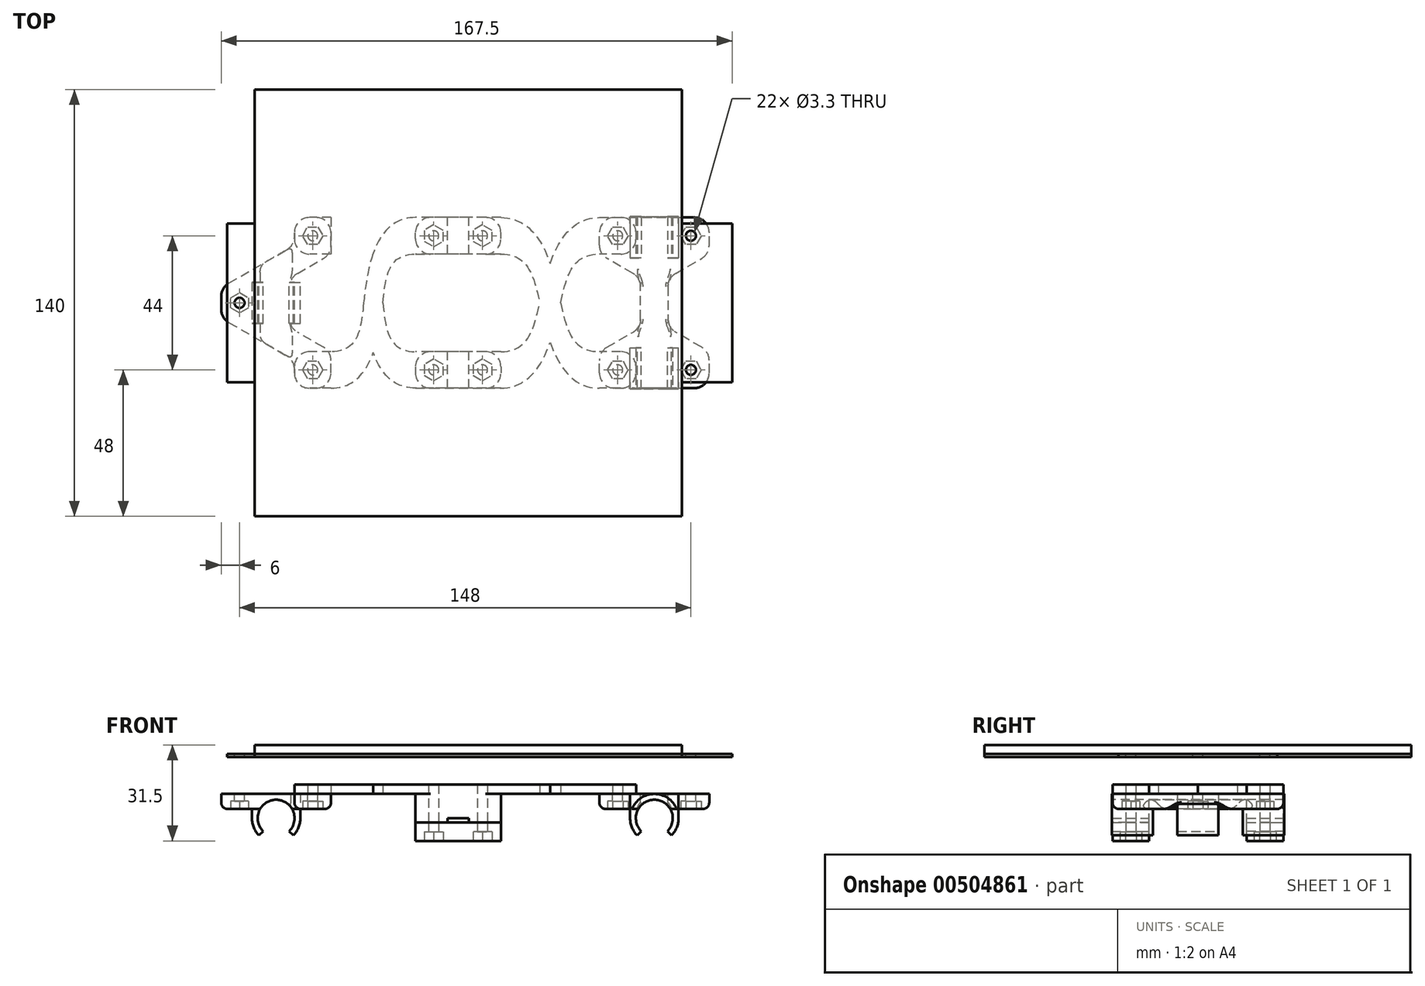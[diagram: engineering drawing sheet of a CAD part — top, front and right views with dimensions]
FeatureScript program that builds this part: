
annotation { "Feature Type Name" : "Feature", "Feature Type Description" : "" }
export const myFeature = defineFeature(function(context is Context, id is Id, definition is map)
    precondition{}
    {
        {
            var Q0;
            Q0=qCreatedBy(makeId("Top.planeOp"),FACE);
            var sketch = newSketch(context, id + "F0", { "sketchPlane" : qUnion([Q0])});
            skLineSegment(sketch, "E0", {"start": v(0, 0) * mm, "end": v(0, -44) * mm});
            skLineSegment(sketch, "E1", {"start": v(0, -44) * mm, "end": v(-9, -44) * mm});
            skLineSegment(sketch, "E2", {"start": v(-9, -44) * mm, "end": v(-9, -96) * mm});
            skLineSegment(sketch, "E3", {"start": v(-9, -96) * mm, "end": v(0, -96) * mm});
            skLineSegment(sketch, "E4", {"start": v(0, -96) * mm, "end": v(0, -140) * mm});
            skLineSegment(sketch, "E5", {"start": v(0, -140) * mm, "end": v(140, -140) * mm});
            skLineSegment(sketch, "E6", {"start": v(140, -140) * mm, "end": v(140, -96) * mm});
            skLineSegment(sketch, "E7", {"start": v(140, -96) * mm, "end": v(156.5, -96) * mm});
            skLineSegment(sketch, "E8", {"start": v(156.5, -96) * mm, "end": v(156.5, -44) * mm});
            skLineSegment(sketch, "E9", {"start": v(156.5, -44) * mm, "end": v(140, -44) * mm});
            skLineSegment(sketch, "E10", {"start": v(140, -44) * mm, "end": v(140, 0) * mm});
            skLineSegment(sketch, "E11", {"start": v(140, 0) * mm, "end": v(0, 0) * mm});
            skLineSegment(sketch, "E12", {"start": v(0, -96) * mm, "end": v(0, -44) * mm});
            skLineSegment(sketch, "E13", {"start": v(140, -96) * mm, "end": v(140, -44) * mm});
            skCircle(sketch, "E14", {"center": v(-5, -70) * mm, "radius": 1.65 * mm});
            skCircle(sketch, "E15", {"center": v(143, -48) * mm, "radius": 1.65 * mm});
            skCircle(sketch, "E16", {"center": v(143, -92) * mm, "radius": 1.65 * mm});
            skSolve(sketch);
        }
        {
            var Q0;
            Q0=makeQuery(id+"F0.imprint","IMPRINT",FACE,{"disambiguationData":[TD([[makeQuery(id+"F0.imprint","IMPRINT",EDGE,{"derivedFrom":sQuery(id+"F0.wireOp",EDGE,"E1")}),1.0]])]});
            var Q1;
            Q1=makeQuery(id+"F0.imprint","IMPRINT",FACE,{"disambiguationData":[TD([[makeQuery(id+"F0.imprint","IMPRINT",EDGE,{"derivedFrom":sQuery(id+"F0.wireOp",EDGE,"E0")}),1.0]])]});
            var Q2;
            Q2=makeQuery(id+"F0.imprint","IMPRINT",FACE,{"disambiguationData":[TD([[makeQuery(id+"F0.imprint","IMPRINT",EDGE,{"derivedFrom":sQuery(id+"F0.wireOp",EDGE,"E7")}),1.0]])]});
            extrude(context, id + "F1", {"entities" : qUnion([Q0, Q1, Q2]), "oppositeDirection" : true, "depth" : 1 * mm});
        }
        {
            var Q0;
            Q0=makeQuery(id+"F0.imprint","IMPRINT",FACE,{"disambiguationData":[TD([[makeQuery(id+"F0.imprint","IMPRINT",EDGE,{"derivedFrom":sQuery(id+"F0.wireOp",EDGE,"E0")}),1.0]])]});
            extrude(context, id + "F2", {"entities" : qUnion([Q0]), "depth" : 3 * mm});
        }
        {
            var Q0;
            Q0=makeQuery(id+"F1.opExtrude","CAP_FACE",FACE,{"disambiguationData":[OSD([sQuery(id+"F0.wireOp",EDGE,"E0"),sQuery(id+"F0.wireOp",EDGE,"E1"),sQuery(id+"F0.wireOp",EDGE,"E2"),sQuery(id+"F0.wireOp",EDGE,"E3"),sQuery(id+"F0.wireOp",EDGE,"E4"),sQuery(id+"F0.wireOp",EDGE,"E5"),sQuery(id+"F0.wireOp",EDGE,"E6"),sQuery(id+"F0.wireOp",EDGE,"E7"),sQuery(id+"F0.wireOp",EDGE,"E8"),sQuery(id+"F0.wireOp",EDGE,"E9"),sQuery(id+"F0.wireOp",EDGE,"E10"),sQuery(id+"F0.wireOp",EDGE,"E11"),sQuery(id+"F0.wireOp",EDGE,"E14"),sQuery(id+"F0.wireOp",EDGE,"E15"),sQuery(id+"F0.wireOp",EDGE,"E16")])],"isStart":false});
            cPlane(context, id + "F3", {"entities" : qUnion([Q0]), "cplaneType" : CPlaneType.OFFSET, "offset" : 12 * mm, "width" : 150 * mm, "height" : 150 * mm});
        }
        {
            var Q0;
            Q0=qCreatedBy(id+"F3.planeOp",FACE);
            var sketch = newSketch(context, id + "F4", { "sketchPlane" : qUnion([Q0])});
            skCircle(sketch, "E17.0", {"center": v(-5, 70) * mm, "radius": 1.65 * mm});
            skCircle(sketch, "E17.1", {"center": v(143, 92) * mm, "radius": 1.65 * mm});
            skCircle(sketch, "E17.2", {"center": v(143, 48) * mm, "radius": 1.65 * mm});
            skCircle(sketch, "E18.cCircle", {"center": v(-5, 70) * mm, "radius": 2.9 * mm, "construction": true});
            skLineSegment(sketch, "E18.0", {"start": v(-2.1, 71.67) * mm, "end": v(-2.1, 68.33) * mm});
            skLineSegment(sketch, "E18.1", {"start": v(-2.1, 68.33) * mm, "end": v(-5, 66.65) * mm});
            skLineSegment(sketch, "E18.2", {"start": v(-5, 66.65) * mm, "end": v(-7.9, 68.33) * mm});
            skLineSegment(sketch, "E18.3", {"start": v(-7.9, 68.33) * mm, "end": v(-7.9, 71.67) * mm});
            skLineSegment(sketch, "E18.4", {"start": v(-7.9, 71.67) * mm, "end": v(-5, 73.35) * mm});
            skLineSegment(sketch, "E18.5", {"start": v(-5, 73.35) * mm, "end": v(-2.1, 71.67) * mm});
            skPoint(sketch, "E18.0.midPoint", {"position": v(-2.1, 70) * mm});
            skCircle(sketch, "E19.cCircle", {"center": v(143, 48) * mm, "radius": 2.9 * mm, "construction": true});
            skLineSegment(sketch, "E19.0", {"start": v(141.33, 50.9) * mm, "end": v(144.67, 50.9) * mm});
            skLineSegment(sketch, "E19.1", {"start": v(144.67, 50.9) * mm, "end": v(146.35, 48) * mm});
            skLineSegment(sketch, "E19.2", {"start": v(146.35, 48) * mm, "end": v(144.67, 45.1) * mm});
            skLineSegment(sketch, "E19.3", {"start": v(144.67, 45.1) * mm, "end": v(141.33, 45.1) * mm});
            skLineSegment(sketch, "E19.4", {"start": v(141.33, 45.1) * mm, "end": v(139.65, 48) * mm});
            skLineSegment(sketch, "E19.5", {"start": v(139.65, 48) * mm, "end": v(141.33, 50.9) * mm});
            skPoint(sketch, "E19.0.midPoint", {"position": v(143, 50.9) * mm});
            skCircle(sketch, "E20.cCircle", {"center": v(143, 92) * mm, "radius": 2.9 * mm, "construction": true});
            skLineSegment(sketch, "E20.0", {"start": v(144.67, 89.1) * mm, "end": v(141.33, 89.1) * mm});
            skLineSegment(sketch, "E20.1", {"start": v(141.33, 89.1) * mm, "end": v(139.65, 92) * mm});
            skLineSegment(sketch, "E20.2", {"start": v(139.65, 92) * mm, "end": v(141.33, 94.9) * mm});
            skLineSegment(sketch, "E20.3", {"start": v(141.33, 94.9) * mm, "end": v(144.67, 94.9) * mm});
            skLineSegment(sketch, "E20.4", {"start": v(144.67, 94.9) * mm, "end": v(146.35, 92) * mm});
            skLineSegment(sketch, "E20.5", {"start": v(146.35, 92) * mm, "end": v(144.67, 89.1) * mm});
            skPoint(sketch, "E20.0.midPoint", {"position": v(143, 89.1) * mm});
            skCircle(sketch, "E21.cCircle", {"center": v(119, 92) * mm, "radius": 2.9 * mm, "construction": true});
            skLineSegment(sketch, "E21.0", {"start": v(120.67, 89.1) * mm, "end": v(117.33, 89.1) * mm});
            skLineSegment(sketch, "E21.1", {"start": v(117.33, 89.1) * mm, "end": v(115.65, 92) * mm});
            skLineSegment(sketch, "E21.2", {"start": v(115.65, 92) * mm, "end": v(117.33, 94.9) * mm});
            skLineSegment(sketch, "E21.3", {"start": v(117.33, 94.9) * mm, "end": v(120.67, 94.9) * mm});
            skLineSegment(sketch, "E21.4", {"start": v(120.67, 94.9) * mm, "end": v(122.35, 92) * mm});
            skLineSegment(sketch, "E21.5", {"start": v(122.35, 92) * mm, "end": v(120.67, 89.1) * mm});
            skPoint(sketch, "E21.0.midPoint", {"position": v(119, 89.1) * mm});
            skCircle(sketch, "E22.cCircle", {"center": v(119, 48) * mm, "radius": 2.9 * mm, "construction": true});
            skLineSegment(sketch, "E22.0", {"start": v(117.33, 50.9) * mm, "end": v(120.67, 50.9) * mm});
            skLineSegment(sketch, "E22.1", {"start": v(120.67, 50.9) * mm, "end": v(122.35, 48) * mm});
            skLineSegment(sketch, "E22.2", {"start": v(122.35, 48) * mm, "end": v(120.67, 45.1) * mm});
            skLineSegment(sketch, "E22.3", {"start": v(120.67, 45.1) * mm, "end": v(117.33, 45.1) * mm});
            skLineSegment(sketch, "E22.4", {"start": v(117.33, 45.1) * mm, "end": v(115.65, 48) * mm});
            skLineSegment(sketch, "E22.5", {"start": v(115.65, 48) * mm, "end": v(117.33, 50.9) * mm});
            skPoint(sketch, "E22.0.midPoint", {"position": v(119, 50.9) * mm});
            skCircle(sketch, "E23.cCircle", {"center": v(19, 92) * mm, "radius": 2.9 * mm, "construction": true});
            skLineSegment(sketch, "E23.0", {"start": v(20.67, 89.1) * mm, "end": v(17.33, 89.1) * mm});
            skLineSegment(sketch, "E23.1", {"start": v(17.33, 89.1) * mm, "end": v(15.65, 92) * mm});
            skLineSegment(sketch, "E23.2", {"start": v(15.65, 92) * mm, "end": v(17.33, 94.9) * mm});
            skLineSegment(sketch, "E23.3", {"start": v(17.33, 94.9) * mm, "end": v(20.67, 94.9) * mm});
            skLineSegment(sketch, "E23.4", {"start": v(20.67, 94.9) * mm, "end": v(22.35, 92) * mm});
            skLineSegment(sketch, "E23.5", {"start": v(22.35, 92) * mm, "end": v(20.67, 89.1) * mm});
            skPoint(sketch, "E23.0.midPoint", {"position": v(19, 89.1) * mm});
            skCircle(sketch, "E24.cCircle", {"center": v(19, 48) * mm, "radius": 2.9 * mm, "construction": true});
            skLineSegment(sketch, "E24.0", {"start": v(17.33, 50.9) * mm, "end": v(20.67, 50.9) * mm});
            skLineSegment(sketch, "E24.1", {"start": v(20.67, 50.9) * mm, "end": v(22.35, 48) * mm});
            skLineSegment(sketch, "E24.2", {"start": v(22.35, 48) * mm, "end": v(20.67, 45.1) * mm});
            skLineSegment(sketch, "E24.3", {"start": v(20.67, 45.1) * mm, "end": v(17.33, 45.1) * mm});
            skLineSegment(sketch, "E24.4", {"start": v(17.33, 45.1) * mm, "end": v(15.65, 48) * mm});
            skLineSegment(sketch, "E24.5", {"start": v(15.65, 48) * mm, "end": v(17.33, 50.9) * mm});
            skPoint(sketch, "E24.0.midPoint", {"position": v(19, 50.9) * mm});
            skLineSegment(sketch, "E25.bottom", {"start": v(125, 136.88) * mm, "end": v(137, 136.88) * mm, "construction": true});
            skLineSegment(sketch, "E25.top", {"start": v(125, 4.25) * mm, "end": v(137, 4.25) * mm, "construction": true});
            skLineSegment(sketch, "E25.left", {"start": v(125, 136.88) * mm, "end": v(125, 4.25) * mm, "construction": true});
            skLineSegment(sketch, "E25.right", {"start": v(137, 136.88) * mm, "end": v(137, 4.25) * mm, "construction": true});
            skLineSegment(sketch, "E26.bottom", {"start": v(1, 146.21) * mm, "end": v(13, 146.21) * mm, "construction": true});
            skLineSegment(sketch, "E26.top", {"start": v(1, -9.43) * mm, "end": v(13, -9.43) * mm, "construction": true});
            skLineSegment(sketch, "E26.left", {"start": v(1, 146.21) * mm, "end": v(1, -9.43) * mm, "construction": true});
            skLineSegment(sketch, "E26.right", {"start": v(13, 146.21) * mm, "end": v(13, -9.43) * mm, "construction": true});
            skLineSegment(sketch, "E27.bottom", {"start": v(125, 101) * mm, "end": v(137, 101) * mm, "construction": true});
            skLineSegment(sketch, "E27.top", {"start": v(125, 82) * mm, "end": v(137, 82) * mm, "construction": true});
            skLineSegment(sketch, "E27.left", {"start": v(125, 101) * mm, "end": v(125, 82) * mm, "construction": true});
            skLineSegment(sketch, "E27.right", {"start": v(137, 101) * mm, "end": v(137, 82) * mm, "construction": true});
            skLineSegment(sketch, "E28.bottom", {"start": v(125, 58) * mm, "end": v(137, 58) * mm, "construction": true});
            skLineSegment(sketch, "E28.top", {"start": v(125, 39) * mm, "end": v(137, 39) * mm, "construction": true});
            skLineSegment(sketch, "E28.left", {"start": v(125, 58) * mm, "end": v(125, 39) * mm, "construction": true});
            skLineSegment(sketch, "E28.right", {"start": v(137, 58) * mm, "end": v(137, 39) * mm, "construction": true});
            skLineSegment(sketch, "E29", {"start": v(-5, 70) * mm, "end": v(43.81, 70) * mm, "construction": true});
            skLineSegment(sketch, "E30.bottom", {"start": v(123.49, 98.25) * mm, "end": v(139, 98.25) * mm, "construction": true});
            skLineSegment(sketch, "E30.top", {"start": v(123.49, 84.75) * mm, "end": v(139, 84.75) * mm, "construction": true});
            skLineSegment(sketch, "E30.left", {"start": v(123.49, 98.25) * mm, "end": v(123.49, 84.75) * mm, "construction": true});
            skLineSegment(sketch, "E30.right", {"start": v(139, 98.25) * mm, "end": v(139, 84.75) * mm, "construction": true});
            skPoint(sketch, "E31", {"position": v(125, 91.5) * mm});
            skPoint(sketch, "E32", {"position": v(123.49, 91.5) * mm});
            skLineSegment(sketch, "E33", {"start": v(149, 98) * mm, "end": v(149, 86) * mm});
            skLineSegment(sketch, "E34", {"start": v(149, 86) * mm, "end": v(135.5, 78.2) * mm});
            skLineSegment(sketch, "E35", {"start": v(135.5, 78.2) * mm, "end": v(135.5, 61.8) * mm});
            skLineSegment(sketch, "E36", {"start": v(135.5, 61.8) * mm, "end": v(149, 54) * mm});
            skLineSegment(sketch, "E37", {"start": v(149, 54) * mm, "end": v(149, 42) * mm});
            skLineSegment(sketch, "E38.MirrorCS", {"start": v(123.49, 41.75) * mm, "end": v(123.49, 55.25) * mm, "construction": true});
            skLineSegment(sketch, "E39.MirrorCS", {"start": v(139, 41.75) * mm, "end": v(139, 55.25) * mm, "construction": true});
            skLineSegment(sketch, "E40.MirrorCS", {"start": v(123.49, 41.75) * mm, "end": v(139, 41.75) * mm, "construction": true});
            skLineSegment(sketch, "E41.MirrorCS", {"start": v(123.49, 55.25) * mm, "end": v(139, 55.25) * mm, "construction": true});
            skPoint(sketch, "E42", {"position": v(131, 136.88) * mm});
            skLineSegment(sketch, "E43", {"start": v(131, 136.88) * mm, "end": v(131, 120.5) * mm, "construction": true});
            skLineSegment(sketch, "E44.MirrorCS", {"start": v(113, 54) * mm, "end": v(113, 42) * mm});
            skLineSegment(sketch, "E45.MirrorCS", {"start": v(126.5, 61.8) * mm, "end": v(113, 54) * mm});
            skLineSegment(sketch, "E46.MirrorCS", {"start": v(126.5, 78.2) * mm, "end": v(126.5, 61.8) * mm});
            skLineSegment(sketch, "E47.MirrorCS", {"start": v(113, 98) * mm, "end": v(113, 86) * mm});
            skLineSegment(sketch, "E48.MirrorCS", {"start": v(113, 86) * mm, "end": v(126.5, 78.2) * mm});
            skPoint(sketch, "E49", {"position": v(149, 92) * mm});
            skLineSegment(sketch, "E50", {"start": v(113, 98) * mm, "end": v(149, 98) * mm});
            skLineSegment(sketch, "E51", {"start": v(113, 42) * mm, "end": v(149, 42) * mm});
            skLineSegment(sketch, "E52", {"start": v(13, 98) * mm, "end": v(25, 98) * mm});
            skLineSegment(sketch, "E53", {"start": v(25, 98) * mm, "end": v(25, 86) * mm});
            skLineSegment(sketch, "E54", {"start": v(25, 86) * mm, "end": v(11.5, 78.2) * mm});
            skLineSegment(sketch, "E55", {"start": v(11.5, 78.2) * mm, "end": v(11.5, 61.8) * mm});
            skLineSegment(sketch, "E56", {"start": v(11.5, 61.8) * mm, "end": v(25, 54) * mm});
            skLineSegment(sketch, "E57", {"start": v(25, 54) * mm, "end": v(25, 42) * mm});
            skLineSegment(sketch, "E58", {"start": v(25, 42) * mm, "end": v(13, 42) * mm});
            skLineSegment(sketch, "E59", {"start": v(-11, 75) * mm, "end": v(-11, 65) * mm});
            skLineSegment(sketch, "E60", {"start": v(-11, 75) * mm, "end": v(13, 88.86) * mm});
            skLineSegment(sketch, "E61", {"start": v(13, 88.86) * mm, "end": v(13, 98) * mm});
            skLineSegment(sketch, "E62", {"start": v(-11, 65) * mm, "end": v(13, 51.14) * mm});
            skLineSegment(sketch, "E63", {"start": v(13, 51.14) * mm, "end": v(13, 42) * mm});
            skSolve(sketch);
        }
        {
            var Q0;
            Q0=makeQuery(id+"F4.imprint","IMPRINT",FACE,{"disambiguationData":[TD([[makeQuery(id+"F4.imprint","IMPRINT",EDGE,{"derivedFrom":sQuery(id+"F4.wireOp",EDGE,"E19.0")}),1.0]])]});
            var Q1;
            Q1=makeQuery(id+"F4.imprint","IMPRINT",FACE,{"disambiguationData":[TD([[makeQuery(id+"F4.imprint","IMPRINT",EDGE,{"derivedFrom":sQuery(id+"F4.wireOp",EDGE,"E22.0")}),-1.0]])]});
            var Q2;
            Q2=makeQuery(id+"F4.imprint","IMPRINT",FACE,{"disambiguationData":[TD([[makeQuery(id+"F4.imprint","IMPRINT",EDGE,{"derivedFrom":sQuery(id+"F4.wireOp",EDGE,"E17.2")}),1.0]])]});
            var Q3;
            Q3=makeQuery(id+"F4.imprint","IMPRINT",FACE,{"disambiguationData":[TD([[makeQuery(id+"F4.imprint","IMPRINT",EDGE,{"derivedFrom":sQuery(id+"F4.wireOp",EDGE,"E17.2")}),-1.0]])]});
            var Q4;
            Q4=makeQuery(id+"F4.imprint","IMPRINT",FACE,{"disambiguationData":[TD([[makeQuery(id+"F4.imprint","IMPRINT",EDGE,{"derivedFrom":sQuery(id+"F4.wireOp",EDGE,"E17.1")}),-1.0]])]});
            var Q5;
            Q5=makeQuery(id+"F4.imprint","IMPRINT",FACE,{"disambiguationData":[TD([[makeQuery(id+"F4.imprint","IMPRINT",EDGE,{"derivedFrom":sQuery(id+"F4.wireOp",EDGE,"E17.1")}),1.0]])]});
            var Q6;
            Q6=makeQuery(id+"F4.imprint","IMPRINT",FACE,{"disambiguationData":[TD([[makeQuery(id+"F4.imprint","IMPRINT",EDGE,{"derivedFrom":sQuery(id+"F4.wireOp",EDGE,"E21.0")}),-1.0]])]});
            var Q7;
            Q7=makeQuery(id+"F4.imprint","IMPRINT",FACE,{"disambiguationData":[TD([[makeQuery(id+"F4.imprint","IMPRINT",EDGE,{"derivedFrom":sQuery(id+"F4.wireOp",EDGE,"E17.0")}),1.0]])]});
            var Q8;
            Q8=makeQuery(id+"F4.imprint","IMPRINT",FACE,{"disambiguationData":[TD([[makeQuery(id+"F4.imprint","IMPRINT",EDGE,{"derivedFrom":sQuery(id+"F4.wireOp",EDGE,"E17.0")}),-1.0]])]});
            var Q9;
            Q9=makeQuery(id+"F4.imprint","IMPRINT",FACE,{"disambiguationData":[TD([[makeQuery(id+"F4.imprint","IMPRINT",EDGE,{"derivedFrom":sQuery(id+"F4.wireOp",EDGE,"E18.0")}),1.0]])]});
            var Q10;
            Q10=makeQuery(id+"F4.imprint","IMPRINT",FACE,{"disambiguationData":[TD([[makeQuery(id+"F4.imprint","IMPRINT",EDGE,{"derivedFrom":sQuery(id+"F4.wireOp",EDGE,"E23.0")}),-1.0]])]});
            var Q11;
            Q11=makeQuery(id+"F4.imprint","IMPRINT",FACE,{"disambiguationData":[TD([[makeQuery(id+"F4.imprint","IMPRINT",EDGE,{"derivedFrom":sQuery(id+"F4.wireOp",EDGE,"E24.0")}),-1.0]])]});
            extrude(context, id + "F5", {"entities" : qUnion([Q0, Q1, Q2, Q3, Q4, Q5, Q6, Q7, Q8, Q9, Q10, Q11]), "depth" : 5 * mm});
        }
        {
            var Q0;
            Q0=makeQuery(id+"F5.opExtrude","SWEPT_FACE",FACE,{"disambiguationData":[OSD([sQuery(id+"F4.wireOp",EDGE,"E51")])]});
            var sketch = newSketch(context, id + "F6", { "sketchPlane" : qUnion([Q0])});
            skCircle(sketch, "E64", {"center": v(-131, -21.05) * mm, "radius": 6.05 * mm});
            skPoint(sketch, "E64.centerSnap0", {"position": v(-131, -18) * mm});
            skCircle(sketch, "E65.0", {"center": v(-131, -21.05) * mm, "radius": 7.95 * mm});
            skLineSegment(sketch, "E66", {"start": v(-138.95, -21.05) * mm, "end": v(-138.95, -13) * mm});
            skLineSegment(sketch, "E67", {"start": v(-123.05, -21.05) * mm, "end": v(-123.05, -13) * mm});
            skLineSegment(sketch, "E68", {"start": v(-131, -21.05) * mm, "end": v(-136.62, -26.67) * mm});
            skLineSegment(sketch, "E69", {"start": v(-131, -21.05) * mm, "end": v(-131, -18) * mm, "construction": true});
            skLineSegment(sketch, "E70.MirrorCS", {"start": v(-131, -21.05) * mm, "end": v(-125.38, -26.67) * mm});
            skSolve(sketch);
        }
        {
            var Q0;
            {var subQ2=sQuery(id+"F6.wireOp",EDGE,"E68");var subQ4=sQuery(id+"F6.wireOp",EDGE,"E64");var subQ8=makeQuery(id+"F6.imprint","INTERSECT",VERTEX,{"derivedFrom":[subQ4,subQ2]});Q0=makeQuery(id+"F6.imprint","IMPRINT",FACE,{"disambiguationData":[TD([[makeQuery(id+"F6.imprint","IMPRINT",EDGE,{"disambiguationData":[TD([[subQ8,1.0]])],"derivedFrom":subQ4}),-1.0]])]});}
            var Q1;
            {var subQ2=sQuery(id+"F6.wireOp",EDGE,"E70.MirrorCS");var subQ6=sQuery(id+"F6.wireOp",EDGE,"E64");var subQ7=makeQuery(id+"F6.imprint","INTERSECT",VERTEX,{"derivedFrom":[subQ6,subQ2]});Q1=makeQuery(id+"F6.imprint","IMPRINT",FACE,{"disambiguationData":[TD([[makeQuery(id+"F6.imprint","IMPRINT",EDGE,{"disambiguationData":[TD([[subQ7,-1.0]])],"derivedFrom":subQ6}),-1.0]])]});}
            var Q2;
            {var subQ1=sQuery(id+"F4.wireOp",EDGE,"E51");var subQ3=makeQuery(id+"F5.opExtrude","CAP_EDGE",EDGE,{"disambiguationData":[OSD([subQ1])],"isStart":false});var subQ5=sQuery(id+"F6.wireOp",EDGE,"E64");var subQ6=makeQuery(id+"F6.imprint","INTERSECT",VERTEX,{"disambiguationData":[OD(0.0)],"derivedFrom":[subQ3,subQ5]});Q2=makeQuery(id+"F6.imprint","IMPRINT",FACE,{"disambiguationData":[TD([[makeQuery(id+"F6.imprint","IMPRINT",EDGE,{"disambiguationData":[TD([[subQ6,1.0]])],"derivedFrom":subQ5}),-1.0]])]});}
            var Q3;
            {var subQ0=sQuery(id+"F6.wireOp",EDGE,"E65.0");var subQ1=sQuery(id+"F4.wireOp",EDGE,"E51");var subQ2=makeQuery(id+"F5.opExtrude","CAP_EDGE",EDGE,{"disambiguationData":[OSD([subQ1])],"isStart":true});var subQ3=makeQuery(id+"F6.imprint","INTERSECT",VERTEX,{"derivedFrom":[subQ2,subQ0]});Q3=makeQuery(id+"F6.imprint","IMPRINT",FACE,{"disambiguationData":[TD([[makeQuery(id+"F6.imprint","IMPRINT",EDGE,{"disambiguationData":[TD([[subQ3,1.0]])],"derivedFrom":subQ0}),-1.0]])]});}
            var Q4;
            {var subQ0=sQuery(id+"F6.wireOp",EDGE,"E67");var subQ1=sQuery(id+"F6.wireOp",EDGE,"E65.0");var subQ2=makeQuery(id+"F6.imprint","INTERSECT",VERTEX,{"derivedFrom":[subQ1,subQ0]});Q4=makeQuery(id+"F6.imprint","IMPRINT",FACE,{"disambiguationData":[TD([[makeQuery(id+"F6.imprint","IMPRINT",EDGE,{"disambiguationData":[TD([[subQ2,-1.0]])],"derivedFrom":subQ1}),-1.0]])]});}
            var Q5;
            {var subQ0=sQuery(id+"F6.wireOp",EDGE,"E66");var subQ1=sQuery(id+"F6.wireOp",EDGE,"E65.0");var subQ2=makeQuery(id+"F6.imprint","INTERSECT",VERTEX,{"derivedFrom":[subQ1,subQ0]});Q5=makeQuery(id+"F6.imprint","IMPRINT",FACE,{"disambiguationData":[TD([[makeQuery(id+"F6.imprint","IMPRINT",EDGE,{"disambiguationData":[TD([[subQ2,1.0]])],"derivedFrom":subQ1}),-1.0]])]});}
            var Q6;
            {var subQ0=sQuery(id+"F6.wireOp",EDGE,"E65.0");var subQ1=sQuery(id+"F4.wireOp",EDGE,"E51");var subQ2=makeQuery(id+"F5.opExtrude","CAP_EDGE",EDGE,{"disambiguationData":[OSD([subQ1])],"isStart":true});var subQ3=makeQuery(id+"F6.imprint","INTERSECT",VERTEX,{"derivedFrom":[subQ2,subQ0]});Q6=makeQuery(id+"F6.imprint","IMPRINT",FACE,{"disambiguationData":[TD([[makeQuery(id+"F6.imprint","IMPRINT",EDGE,{"disambiguationData":[TD([[subQ3,-1.0]])],"derivedFrom":subQ0}),-1.0]])]});}
            var Q7;
            {var subQ1=sQuery(id+"F4.wireOp",EDGE,"E51");var subQ6=makeQuery(id+"F5.opExtrude","CAP_EDGE",EDGE,{"disambiguationData":[OSD([subQ1])],"isStart":false});var subQ9=sQuery(id+"F6.wireOp",EDGE,"E65.0");var subQ10=makeQuery(id+"F6.imprint","INTERSECT",VERTEX,{"disambiguationData":[OD(0.0)],"derivedFrom":[subQ6,subQ9]});Q7=makeQuery(id+"F6.imprint","IMPRINT",FACE,{"disambiguationData":[TD([[makeQuery(id+"F6.imprint","IMPRINT",EDGE,{"disambiguationData":[TD([[subQ10,-1.0]])],"derivedFrom":subQ9}),-1.0]])]});}
            var Q8;
            Q8=sQuery(id+"F4.wireOp",VERTEX,"E40.MirrorCS.end");
            var Q9;
            Q9=sQuery(id+"F4.wireOp",VERTEX,"E39.MirrorCS.end");
            extrude(context, id + "F7", {"entities" : qUnion([Q0, Q1, Q2, Q3, Q4, Q5, Q6, Q7]), "operationType" : NewBodyOperationType.ADD, "endBound" : BoundingType.UP_TO_VERTEX, "endBoundEntityVertex" : qUnion([Q8]), "depth" : 25 * mm, "hasSecondDirection" : true, "secondDirectionBound" : SecondDirectionBoundingType.UP_TO_VERTEX, "secondDirectionOppositeDirection" : true, "secondDirectionBoundEntityVertex" : qUnion([Q9]), "secondDirectionDepth" : 25 * mm});
        }
        {
            var Q0;
            {var subQ0=sQuery(id+"F6.wireOp",EDGE,"E64");var subQ1=makeQuery(id+"F5.opExtrude","CAP_EDGE",EDGE,{"disambiguationData":[OSD([sQuery(id+"F4.wireOp",EDGE,"E51")])],"isStart":false});var subQ2=makeQuery(id+"F6.imprint","INTERSECT",VERTEX,{"disambiguationData":[OD(0.0)],"derivedFrom":[subQ1,subQ0]});Q0=makeQuery(id+"F6.imprint","IMPRINT",FACE,{"disambiguationData":[TD([[makeQuery(id+"F6.imprint","IMPRINT",EDGE,{"disambiguationData":[TD([[subQ2,-1.0]])],"derivedFrom":subQ0}),1.0]])]});}
            var Q1;
            {var subQ0=sQuery(id+"F6.wireOp",EDGE,"E64");var subQ1=makeQuery(id+"F5.opExtrude","CAP_EDGE",EDGE,{"disambiguationData":[OSD([sQuery(id+"F4.wireOp",EDGE,"E51")])],"isStart":false});var subQ2=makeQuery(id+"F6.imprint","INTERSECT",VERTEX,{"disambiguationData":[OD(0.0)],"derivedFrom":[subQ1,subQ0]});Q1=makeQuery(id+"F6.imprint","IMPRINT",FACE,{"disambiguationData":[TD([[makeQuery(id+"F6.imprint","IMPRINT",EDGE,{"disambiguationData":[TD([[subQ2,1.0]])],"derivedFrom":subQ0}),1.0]])]});}
            extrude(context, id + "F8", {"entities" : qUnion([Q0, Q1]), "operationType" : NewBodyOperationType.REMOVE, "endBound" : BoundingType.THROUGH_ALL, "oppositeDirection" : true, "depth" : 25 * mm});
        }
        {
            var Q0;
            Q0=makeQuery(id+"F5.opExtrude","SWEPT_EDGE",EDGE,{"disambiguationData":[OSD([sQuery(id+"F4.wireOp",EDGE,"E37"),sQuery(id+"F4.wireOp",EDGE,"E51")])]});
            var Q1;
            Q1=makeQuery(id+"F5.opExtrude","SWEPT_EDGE",EDGE,{"disambiguationData":[OSD([sQuery(id+"F4.wireOp",EDGE,"E36"),sQuery(id+"F4.wireOp",EDGE,"E37")])]});
            var Q2;
            Q2=makeQuery(id+"F5.opExtrude","SWEPT_EDGE",EDGE,{"disambiguationData":[OSD([sQuery(id+"F4.wireOp",EDGE,"E35"),sQuery(id+"F4.wireOp",EDGE,"E36")])]});
            var Q3;
            Q3=makeQuery(id+"F5.opExtrude","SWEPT_EDGE",EDGE,{"disambiguationData":[OSD([sQuery(id+"F4.wireOp",EDGE,"E44.MirrorCS"),sQuery(id+"F4.wireOp",EDGE,"E51")])]});
            var Q4;
            Q4=makeQuery(id+"F5.opExtrude","SWEPT_EDGE",EDGE,{"disambiguationData":[OSD([sQuery(id+"F4.wireOp",EDGE,"E44.MirrorCS"),sQuery(id+"F4.wireOp",EDGE,"E45.MirrorCS")])]});
            var Q5;
            Q5=makeQuery(id+"F5.opExtrude","SWEPT_EDGE",EDGE,{"disambiguationData":[OSD([sQuery(id+"F4.wireOp",EDGE,"E45.MirrorCS"),sQuery(id+"F4.wireOp",EDGE,"E46.MirrorCS")])]});
            var Q6;
            Q6=makeQuery(id+"F5.opExtrude","SWEPT_EDGE",EDGE,{"disambiguationData":[OSD([sQuery(id+"F4.wireOp",EDGE,"E46.MirrorCS"),sQuery(id+"F4.wireOp",EDGE,"E48.MirrorCS")])]});
            var Q7;
            Q7=makeQuery(id+"F5.opExtrude","SWEPT_EDGE",EDGE,{"disambiguationData":[OSD([sQuery(id+"F4.wireOp",EDGE,"E47.MirrorCS"),sQuery(id+"F4.wireOp",EDGE,"E48.MirrorCS")])]});
            var Q8;
            Q8=makeQuery(id+"F5.opExtrude","SWEPT_EDGE",EDGE,{"disambiguationData":[OSD([sQuery(id+"F4.wireOp",EDGE,"E47.MirrorCS"),sQuery(id+"F4.wireOp",EDGE,"E50")])]});
            var Q9;
            Q9=makeQuery(id+"F5.opExtrude","SWEPT_EDGE",EDGE,{"disambiguationData":[OSD([sQuery(id+"F4.wireOp",EDGE,"E33"),sQuery(id+"F4.wireOp",EDGE,"E34")])]});
            var Q10;
            Q10=makeQuery(id+"F5.opExtrude","SWEPT_EDGE",EDGE,{"disambiguationData":[OSD([sQuery(id+"F4.wireOp",EDGE,"E34"),sQuery(id+"F4.wireOp",EDGE,"E35")])]});
            var Q11;
            Q11=makeQuery(id+"F5.opExtrude","SWEPT_EDGE",EDGE,{"disambiguationData":[OSD([sQuery(id+"F4.wireOp",EDGE,"E33"),sQuery(id+"F4.wireOp",EDGE,"E50")])]});
            var Q12;
            Q12=makeQuery(id+"F5.opExtrude","SWEPT_EDGE",EDGE,{"disambiguationData":[OSD([sQuery(id+"F4.wireOp",EDGE,"E59"),sQuery(id+"F4.wireOp",EDGE,"E62")])]});
            var Q13;
            Q13=makeQuery(id+"F5.opExtrude","SWEPT_EDGE",EDGE,{"disambiguationData":[OSD([sQuery(id+"F4.wireOp",EDGE,"E59"),sQuery(id+"F4.wireOp",EDGE,"E60")])]});
            var Q14;
            Q14=makeQuery(id+"F5.opExtrude","SWEPT_EDGE",EDGE,{"disambiguationData":[OSD([sQuery(id+"F4.wireOp",EDGE,"E62"),sQuery(id+"F4.wireOp",EDGE,"E63")])]});
            var Q15;
            Q15=makeQuery(id+"F5.opExtrude","SWEPT_EDGE",EDGE,{"disambiguationData":[OSD([sQuery(id+"F4.wireOp",EDGE,"E58"),sQuery(id+"F4.wireOp",EDGE,"E63")])]});
            var Q16;
            Q16=makeQuery(id+"F5.opExtrude","SWEPT_EDGE",EDGE,{"disambiguationData":[OSD([sQuery(id+"F4.wireOp",EDGE,"E57"),sQuery(id+"F4.wireOp",EDGE,"E58")])]});
            var Q17;
            Q17=makeQuery(id+"F5.opExtrude","SWEPT_EDGE",EDGE,{"disambiguationData":[OSD([sQuery(id+"F4.wireOp",EDGE,"E56"),sQuery(id+"F4.wireOp",EDGE,"E57")])]});
            var Q18;
            Q18=makeQuery(id+"F5.opExtrude","SWEPT_EDGE",EDGE,{"disambiguationData":[OSD([sQuery(id+"F4.wireOp",EDGE,"E55"),sQuery(id+"F4.wireOp",EDGE,"E56")])]});
            var Q19;
            Q19=makeQuery(id+"F5.opExtrude","SWEPT_EDGE",EDGE,{"disambiguationData":[OSD([sQuery(id+"F4.wireOp",EDGE,"E54"),sQuery(id+"F4.wireOp",EDGE,"E55")])]});
            var Q20;
            Q20=makeQuery(id+"F5.opExtrude","SWEPT_EDGE",EDGE,{"disambiguationData":[OSD([sQuery(id+"F4.wireOp",EDGE,"E53"),sQuery(id+"F4.wireOp",EDGE,"E54")])]});
            var Q21;
            Q21=makeQuery(id+"F5.opExtrude","SWEPT_EDGE",EDGE,{"disambiguationData":[OSD([sQuery(id+"F4.wireOp",EDGE,"E52"),sQuery(id+"F4.wireOp",EDGE,"E53")])]});
            var Q22;
            Q22=makeQuery(id+"F5.opExtrude","SWEPT_EDGE",EDGE,{"disambiguationData":[OSD([sQuery(id+"F4.wireOp",EDGE,"E60"),sQuery(id+"F4.wireOp",EDGE,"E61")])]});
            var Q23;
            Q23=makeQuery(id+"F5.opExtrude","SWEPT_EDGE",EDGE,{"disambiguationData":[OSD([sQuery(id+"F4.wireOp",EDGE,"E52"),sQuery(id+"F4.wireOp",EDGE,"E61")])]});
            fillet(context, id + "F9", {"entities" : qUnion([Q0, Q1, Q2, Q3, Q4, Q5, Q6, Q7, Q8, Q9, Q10, Q11, Q12, Q13, Q14, Q15, Q16, Q17, Q18, Q19, Q20, Q21, Q22, Q23]), "radius" : 5 * mm, "tangentPropagation" : true, "allowEdgeOverflow" : false});
        }
        {
            var Q0;
            Q0=sQuery(id+"F4.wireOp",VERTEX,"E17.2.center");
            var Q1;
            Q1=sQuery(id+"F4.wireOp",VERTEX,"E17.1.center");
            var Q2;
            Q2=sQuery(id+"F4.wireOp",VERTEX,"E21.cCircle.center");
            var Q3;
            Q3=sQuery(id+"F4.wireOp",VERTEX,"E22.cCircle.center");
            var Q4;
            Q4=sQuery(id+"F4.wireOp",VERTEX,"E24.cCircle.center");
            var Q5;
            Q5=sQuery(id+"F4.wireOp",VERTEX,"E18.cCircle.center");
            var Q6;
            Q6=sQuery(id+"F4.wireOp",VERTEX,"E23.cCircle.center");
            var Q7;
            Q7=makeQuery(id+"F5.opExtrude","SWEPT_BODY",BODY,{"disambiguationData":[OSD([sQuery(id+"F4.wireOp",EDGE,"E33"),sQuery(id+"F4.wireOp",EDGE,"E34"),sQuery(id+"F4.wireOp",EDGE,"E35"),sQuery(id+"F4.wireOp",EDGE,"E36"),sQuery(id+"F4.wireOp",EDGE,"E37"),sQuery(id+"F4.wireOp",EDGE,"E44.MirrorCS"),sQuery(id+"F4.wireOp",EDGE,"E45.MirrorCS"),sQuery(id+"F4.wireOp",EDGE,"E46.MirrorCS"),sQuery(id+"F4.wireOp",EDGE,"E47.MirrorCS"),sQuery(id+"F4.wireOp",EDGE,"E48.MirrorCS"),sQuery(id+"F4.wireOp",EDGE,"E50"),sQuery(id+"F4.wireOp",EDGE,"E51")])]});
            var Q8;
            Q8=makeQuery(id+"F5.opExtrude","SWEPT_BODY",BODY,{"disambiguationData":[OSD([sQuery(id+"F4.wireOp",EDGE,"E52"),sQuery(id+"F4.wireOp",EDGE,"E53"),sQuery(id+"F4.wireOp",EDGE,"E54"),sQuery(id+"F4.wireOp",EDGE,"E55"),sQuery(id+"F4.wireOp",EDGE,"E56"),sQuery(id+"F4.wireOp",EDGE,"E57"),sQuery(id+"F4.wireOp",EDGE,"E58"),sQuery(id+"F4.wireOp",EDGE,"E59"),sQuery(id+"F4.wireOp",EDGE,"E60"),sQuery(id+"F4.wireOp",EDGE,"E61"),sQuery(id+"F4.wireOp",EDGE,"E62"),sQuery(id+"F4.wireOp",EDGE,"E63")])]});
            hole(context, id + "F10", {"style" : HoleStyle.SIMPLE, "endStyle" : HoleEndStyle.THROUGH, "oppositeDirection" : true, "standardTappedOrClearance" : lookupTablePath({ "standard" : "ISO", "fit" : "Normal", "size" : "M3", "type" : "Clearance" }), "standardBlindInLast" : lookupTablePath({ "fit" : "Standard", "standard" : "ISO", "size" : "M3", "type" : "Clearance" }), "holeDiameter" : 3.3 * mm, "isTappedThrough" : true, "tappedDepth" : 12 * mm, "tapClearance" : 3, "locations" : qUnion([Q0, Q1, Q2, Q3, Q4, Q5, Q6]), "scope" : qUnion([Q7, Q8])});
        }
        {
            var Q0;
            Q0=makeQuery(id+"F5.opExtrude","SWEPT_FACE",FACE,{"disambiguationData":[OSD([sQuery(id+"F4.wireOp",EDGE,"E50")])]});
            var sketch = newSketch(context, id + "F11", { "sketchPlane" : qUnion([Q0])});
            skCircle(sketch, "E71.0", {"center": v(131, -21.05) * mm, "radius": 7.95 * mm});
            skCircle(sketch, "E72.0", {"center": v(131, -21.05) * mm, "radius": 6.05 * mm});
            skLineSegment(sketch, "E73.0", {"start": v(131, -21.05) * mm, "end": v(125.38, -26.67) * mm});
            skLineSegment(sketch, "E73.1", {"start": v(131, -21.05) * mm, "end": v(136.62, -26.67) * mm});
            skLineSegment(sketch, "E73.2", {"start": v(123.05, -21.05) * mm, "end": v(123.05, -13) * mm});
            skLineSegment(sketch, "E73.3", {"start": v(138.95, -21.05) * mm, "end": v(138.95, -13) * mm});
            skSolve(sketch);
        }
        {
            var Q0;
            {var subQ0=sQuery(id+"F11.wireOp",EDGE,"E73.2");var subQ1=sQuery(id+"F11.wireOp",EDGE,"E71.0");var subQ2=makeQuery(id+"F11.imprint","INTERSECT",VERTEX,{"derivedFrom":[subQ1,subQ0]});Q0=makeQuery(id+"F11.imprint","IMPRINT",FACE,{"disambiguationData":[TD([[makeQuery(id+"F11.imprint","IMPRINT",EDGE,{"disambiguationData":[TD([[subQ2,-1.0]])],"derivedFrom":subQ1}),1.0]])]});}
            var Q1;
            {var subQ1=sQuery(id+"F4.wireOp",EDGE,"E50");var subQ2=makeQuery(id+"F5.opExtrude","CAP_EDGE",EDGE,{"disambiguationData":[OSD([subQ1])],"isStart":true});var subQ8=sQuery(id+"F11.wireOp",EDGE,"E73.2");var subQ10=makeQuery(id+"F11.imprint","INTERSECT",VERTEX,{"derivedFrom":[subQ2,subQ8]});Q1=makeQuery(id+"F11.imprint","IMPRINT",FACE,{"disambiguationData":[TD([[makeQuery(id+"F11.imprint","IMPRINT",EDGE,{"disambiguationData":[TD([[subQ10,-1.0]])],"derivedFrom":subQ2}),-1.0]])]});}
            var Q2;
            {var subQ0=sQuery(id+"F11.wireOp",EDGE,"E73.3");var subQ1=sQuery(id+"F11.wireOp",EDGE,"E71.0");var subQ2=makeQuery(id+"F11.imprint","INTERSECT",VERTEX,{"derivedFrom":[subQ1,subQ0]});Q2=makeQuery(id+"F11.imprint","IMPRINT",FACE,{"disambiguationData":[TD([[makeQuery(id+"F11.imprint","IMPRINT",EDGE,{"disambiguationData":[TD([[subQ2,1.0]])],"derivedFrom":subQ1}),1.0]])]});}
            var Q3;
            {var subQ1=sQuery(id+"F4.wireOp",EDGE,"E50");var subQ2=makeQuery(id+"F5.opExtrude","CAP_EDGE",EDGE,{"disambiguationData":[OSD([subQ1])],"isStart":true});var subQ8=sQuery(id+"F11.wireOp",EDGE,"E73.3");var subQ9=makeQuery(id+"F11.imprint","INTERSECT",VERTEX,{"derivedFrom":[subQ2,subQ8]});Q3=makeQuery(id+"F11.imprint","IMPRINT",FACE,{"disambiguationData":[TD([[makeQuery(id+"F11.imprint","IMPRINT",EDGE,{"disambiguationData":[TD([[subQ9,1.0]])],"derivedFrom":subQ2}),-1.0]])]});}
            var Q4;
            {var subQ4=sQuery(id+"F4.wireOp",EDGE,"E50");var subQ12=sQuery(id+"F11.wireOp",EDGE,"E71.0");var subQ16=makeQuery(id+"F11.imprint","INTERSECT",VERTEX,{"derivedFrom":[makeQuery(id+"F5.opExtrude","CAP_EDGE",EDGE,{"disambiguationData":[OSD([subQ4])],"isStart":true}),subQ12]});Q4=makeQuery(id+"F11.imprint","IMPRINT",FACE,{"disambiguationData":[TD([[makeQuery(id+"F11.imprint","IMPRINT",EDGE,{"disambiguationData":[TD([[subQ16,1.0]])],"derivedFrom":subQ12}),-1.0]])]});}
            var Q5;
            {var subQ0=sQuery(id+"F11.wireOp",EDGE,"E73.1");var subQ1=sQuery(id+"F11.wireOp",EDGE,"E71.0");var subQ2=makeQuery(id+"F11.imprint","INTERSECT",VERTEX,{"derivedFrom":[subQ1,subQ0]});Q5=makeQuery(id+"F11.imprint","IMPRINT",FACE,{"disambiguationData":[TD([[makeQuery(id+"F11.imprint","IMPRINT",EDGE,{"disambiguationData":[TD([[subQ2,1.0]])],"derivedFrom":subQ1}),-1.0]])]});}
            var Q6;
            {var subQ0=sQuery(id+"F11.wireOp",EDGE,"E73.0");var subQ1=sQuery(id+"F11.wireOp",EDGE,"E71.0");var subQ2=makeQuery(id+"F11.imprint","INTERSECT",VERTEX,{"derivedFrom":[subQ1,subQ0]});Q6=makeQuery(id+"F11.imprint","IMPRINT",FACE,{"disambiguationData":[TD([[makeQuery(id+"F11.imprint","IMPRINT",EDGE,{"disambiguationData":[TD([[subQ2,-1.0]])],"derivedFrom":subQ1}),-1.0]])]});}
            var Q7;
            {var subQ0=sQuery(id+"F11.wireOp",EDGE,"E71.0");var subQ3=sQuery(id+"F4.wireOp",EDGE,"E47.MirrorCS");var subQ4=sQuery(id+"F4.wireOp",EDGE,"E50");var subQ9=makeQuery(id+"F5.opExtrude","CAP_EDGE",EDGE,{"disambiguationData":[OSD([subQ4])],"isStart":false});var subQ10=makeQuery(id+"F8.boolean.opBoolean","SPLIT",EDGE,{"disambiguationData":[TD([makeQuery(id+"F5.opExtrude","SWEPT_FACE",FACE,{"disambiguationData":[OSD([subQ3])]})])],"derivedFrom":subQ9});var subQ11=makeQuery(id+"F11.imprint","INTERSECT",VERTEX,{"derivedFrom":[subQ10,subQ0]});Q7=makeQuery(id+"F11.imprint","IMPRINT",FACE,{"disambiguationData":[TD([[makeQuery(id+"F11.imprint","IMPRINT",EDGE,{"disambiguationData":[TD([[subQ11,-1.0]])],"derivedFrom":subQ0}),-1.0]])]});}
            var Q8;
            Q8=sQuery(id+"F4.wireOp",VERTEX,"E30.bottom.end");
            var Q9;
            Q9=sQuery(id+"F4.wireOp",VERTEX,"E30.right.end");
            extrude(context, id + "F12", {"entities" : qUnion([Q0, Q1, Q2, Q3, Q4, Q5, Q6, Q7]), "operationType" : NewBodyOperationType.ADD, "endBound" : BoundingType.UP_TO_VERTEX, "endBoundEntityVertex" : qUnion([Q8]), "depth" : 25 * mm, "hasSecondDirection" : true, "secondDirectionBound" : SecondDirectionBoundingType.UP_TO_VERTEX, "secondDirectionOppositeDirection" : true, "secondDirectionBoundEntityVertex" : qUnion([Q9]), "secondDirectionDepth" : 25 * mm});
        }
        {
            var Q0;
            {var subQ0=sQuery(id+"F4.wireOp",EDGE,"E51");var subQ1=sQuery(id+"F4.wireOp",EDGE,"E37");Q0=makeQuery(id+"F7.boolean.opBoolean","SPLIT",EDGE,{"disambiguationData":[TD([makeQuery(id+"F5.opExtrude","SWEPT_FACE",FACE,{"disambiguationData":[OSD([subQ1])]})])],"derivedFrom":makeQuery(id+"F5.opExtrude","CAP_EDGE",EDGE,{"disambiguationData":[OSD([subQ0])],"isStart":false})});}
            var Q1;
            {var subQ0=sQuery(id+"F4.wireOp",EDGE,"E50");var subQ1=sQuery(id+"F4.wireOp",EDGE,"E33");Q1=makeQuery(id+"F8.boolean.opBoolean","SPLIT",EDGE,{"disambiguationData":[TD([makeQuery(id+"F5.opExtrude","SWEPT_FACE",FACE,{"disambiguationData":[OSD([subQ1])]})])],"derivedFrom":makeQuery(id+"F5.opExtrude","CAP_EDGE",EDGE,{"disambiguationData":[OSD([subQ0])],"isStart":false})});}
            var Q2;
            Q2=makeQuery(id+"F5.opExtrude","CAP_EDGE",EDGE,{"disambiguationData":[OSD([sQuery(id+"F4.wireOp",EDGE,"E47.MirrorCS")])],"isStart":false});
            var Q3;
            Q3=makeQuery(id+"F5.opExtrude","CAP_EDGE",EDGE,{"disambiguationData":[OSD([sQuery(id+"F4.wireOp",EDGE,"E44.MirrorCS")])],"isStart":false});
            var Q4;
            Q4=makeQuery(id+"F5.opExtrude","CAP_EDGE",EDGE,{"disambiguationData":[OSD([sQuery(id+"F4.wireOp",EDGE,"E60")])],"isStart":false});
            fillet(context, id + "F13", {"entities" : qUnion([Q0, Q1, Q2, Q3, Q4]), "radius" : 2 * mm, "tangentPropagation" : true, "allowEdgeOverflow" : false});
        }
        {
            var Q0;
            Q0=makeQuery(id+"F8.boolean.opBoolean","INTERSECT",EDGE,{"derivedFrom":[makeQuery(id+"F5.opExtrude","SWEPT_FACE",FACE,{"disambiguationData":[OSD([sQuery(id+"F4.wireOp",EDGE,"E35")])]}),makeQuery(id+"F8.opExtrude","SWEPT_FACE",FACE,{"disambiguationData":[OSD([sQuery(id+"F6.wireOp",EDGE,"E64")])]})]});
            var Q1;
            Q1=makeQuery(id+"F8.boolean.opBoolean","INTERSECT",EDGE,{"derivedFrom":[makeQuery(id+"F5.opExtrude","SWEPT_FACE",FACE,{"disambiguationData":[OSD([sQuery(id+"F4.wireOp",EDGE,"E46.MirrorCS")])]}),makeQuery(id+"F8.opExtrude","SWEPT_FACE",FACE,{"disambiguationData":[OSD([sQuery(id+"F6.wireOp",EDGE,"E64")])]})]});
            var Q2;
            Q2=makeQuery(id+"F8.boolean.opBoolean","INTERSECT",EDGE,{"disambiguationData":[OD(3.0)],"derivedFrom":[makeQuery(id+"F5.opExtrude","CAP_FACE",FACE,{"disambiguationData":[OSD([sQuery(id+"F4.wireOp",EDGE,"E33"),sQuery(id+"F4.wireOp",EDGE,"E34"),sQuery(id+"F4.wireOp",EDGE,"E35"),sQuery(id+"F4.wireOp",EDGE,"E36"),sQuery(id+"F4.wireOp",EDGE,"E37"),sQuery(id+"F4.wireOp",EDGE,"E44.MirrorCS"),sQuery(id+"F4.wireOp",EDGE,"E45.MirrorCS"),sQuery(id+"F4.wireOp",EDGE,"E46.MirrorCS"),sQuery(id+"F4.wireOp",EDGE,"E47.MirrorCS"),sQuery(id+"F4.wireOp",EDGE,"E48.MirrorCS"),sQuery(id+"F4.wireOp",EDGE,"E50"),sQuery(id+"F4.wireOp",EDGE,"E51")])],"isStart":false}),makeQuery(id+"F8.opExtrude","SWEPT_FACE",FACE,{"disambiguationData":[OSD([sQuery(id+"F6.wireOp",EDGE,"E64")])]})]});
            var Q3;
            {var subQ0=sQuery(id+"F6.wireOp",EDGE,"E64");var subQ1=makeQuery(id+"F8.opExtrude","SWEPT_FACE",FACE,{"disambiguationData":[OSD([subQ0])]});var subQ2=makeQuery(id+"F7.opExtrude","SWEPT_FACE",FACE,{"disambiguationData":[OSD([subQ0])]});var subQ3=sQuery(id+"F4.wireOp",EDGE,"E50");var subQ4=sQuery(id+"F4.wireOp",EDGE,"E48.MirrorCS");var subQ5=sQuery(id+"F4.wireOp",EDGE,"E47.MirrorCS");var subQ6=sQuery(id+"F4.wireOp",EDGE,"E46.MirrorCS");Q3=makeQuery(id+"F13.opFillet","BLEND_EDGE",EDGE,{"blendedFrom":[makeQuery(id+"F9.opFillet","BLEND_EDGE",EDGE,{"blendedFrom":[makeQuery(id+"F5.opExtrude","SWEPT_EDGE",EDGE,{"disambiguationData":[OSD([subQ6,subQ4])]}),makeQuery(id+"F8.boolean.opBoolean","SPLIT",FACE,{"disambiguationData":[TD([makeQuery(id+"F5.opExtrude","SWEPT_FACE",FACE,{"disambiguationData":[OSD([subQ5])]})])],"derivedFrom":makeQuery(id+"F5.opExtrude","CAP_FACE",FACE,{"disambiguationData":[OSD([sQuery(id+"F4.wireOp",EDGE,"E33"),sQuery(id+"F4.wireOp",EDGE,"E34"),sQuery(id+"F4.wireOp",EDGE,"E35"),sQuery(id+"F4.wireOp",EDGE,"E36"),sQuery(id+"F4.wireOp",EDGE,"E37"),sQuery(id+"F4.wireOp",EDGE,"E44.MirrorCS"),sQuery(id+"F4.wireOp",EDGE,"E45.MirrorCS"),subQ6,subQ5,subQ4,subQ3,sQuery(id+"F4.wireOp",EDGE,"E51")])],"isStart":false})})],"blendedInto":[makeQuery(id+"F8.boolean.opBoolean","SPLIT",FACE,{"disambiguationData":[TD([makeQuery(id+"F5.opExtrude","SWEPT_FACE",FACE,{"disambiguationData":[OSD([subQ5])]})])],"derivedFrom":makeQuery(id+"F5.opExtrude","CAP_FACE",FACE,{"disambiguationData":[OSD([sQuery(id+"F4.wireOp",EDGE,"E33"),sQuery(id+"F4.wireOp",EDGE,"E34"),sQuery(id+"F4.wireOp",EDGE,"E35"),sQuery(id+"F4.wireOp",EDGE,"E36"),sQuery(id+"F4.wireOp",EDGE,"E37"),sQuery(id+"F4.wireOp",EDGE,"E44.MirrorCS"),sQuery(id+"F4.wireOp",EDGE,"E45.MirrorCS"),subQ6,subQ5,subQ4,subQ3,sQuery(id+"F4.wireOp",EDGE,"E51")])],"isStart":false})})]}),makeQuery(id+"F12.boolean.opBoolean","MERGE",FACE,{"derivedFrom":[makeQuery(id+"F8.boolean.opBoolean","MERGE",FACE,{"derivedFrom":[subQ2,subQ1]}),makeQuery(id+"F12.opExtrude","SWEPT_FACE",FACE,{"disambiguationData":[OSD([sQuery(id+"F11.wireOp",EDGE,"E72.0")])]})]})],"blendedInto":[makeQuery(id+"F12.boolean.opBoolean","MERGE",FACE,{"derivedFrom":[makeQuery(id+"F8.boolean.opBoolean","MERGE",FACE,{"derivedFrom":[subQ2,subQ1]}),makeQuery(id+"F12.opExtrude","SWEPT_FACE",FACE,{"disambiguationData":[OSD([sQuery(id+"F11.wireOp",EDGE,"E72.0")])]})]})]});}
            var Q4;
            Q4=makeQuery(id+"F8.boolean.opBoolean","INTERSECT",EDGE,{"disambiguationData":[OD(2.0)],"derivedFrom":[makeQuery(id+"F5.opExtrude","CAP_FACE",FACE,{"disambiguationData":[OSD([sQuery(id+"F4.wireOp",EDGE,"E33"),sQuery(id+"F4.wireOp",EDGE,"E34"),sQuery(id+"F4.wireOp",EDGE,"E35"),sQuery(id+"F4.wireOp",EDGE,"E36"),sQuery(id+"F4.wireOp",EDGE,"E37"),sQuery(id+"F4.wireOp",EDGE,"E44.MirrorCS"),sQuery(id+"F4.wireOp",EDGE,"E45.MirrorCS"),sQuery(id+"F4.wireOp",EDGE,"E46.MirrorCS"),sQuery(id+"F4.wireOp",EDGE,"E47.MirrorCS"),sQuery(id+"F4.wireOp",EDGE,"E48.MirrorCS"),sQuery(id+"F4.wireOp",EDGE,"E50"),sQuery(id+"F4.wireOp",EDGE,"E51")])],"isStart":false}),makeQuery(id+"F8.opExtrude","SWEPT_FACE",FACE,{"disambiguationData":[OSD([sQuery(id+"F6.wireOp",EDGE,"E64")])]})]});
            var Q5;
            {var subQ0=sQuery(id+"F6.wireOp",EDGE,"E64");var subQ1=makeQuery(id+"F8.opExtrude","SWEPT_FACE",FACE,{"disambiguationData":[OSD([subQ0])]});var subQ2=makeQuery(id+"F7.opExtrude","SWEPT_FACE",FACE,{"disambiguationData":[OSD([subQ0])]});var subQ3=sQuery(id+"F4.wireOp",EDGE,"E50");var subQ4=sQuery(id+"F4.wireOp",EDGE,"E34");var subQ5=sQuery(id+"F4.wireOp",EDGE,"E33");var subQ6=sQuery(id+"F4.wireOp",EDGE,"E35");Q5=makeQuery(id+"F13.opFillet","BLEND_EDGE",EDGE,{"blendedFrom":[makeQuery(id+"F9.opFillet","BLEND_EDGE",EDGE,{"blendedFrom":[makeQuery(id+"F5.opExtrude","SWEPT_EDGE",EDGE,{"disambiguationData":[OSD([subQ4,subQ6])]}),makeQuery(id+"F8.boolean.opBoolean","SPLIT",FACE,{"disambiguationData":[TD([makeQuery(id+"F5.opExtrude","SWEPT_FACE",FACE,{"disambiguationData":[OSD([subQ5])]})])],"derivedFrom":makeQuery(id+"F5.opExtrude","CAP_FACE",FACE,{"disambiguationData":[OSD([subQ5,subQ4,subQ6,sQuery(id+"F4.wireOp",EDGE,"E36"),sQuery(id+"F4.wireOp",EDGE,"E37"),sQuery(id+"F4.wireOp",EDGE,"E44.MirrorCS"),sQuery(id+"F4.wireOp",EDGE,"E45.MirrorCS"),sQuery(id+"F4.wireOp",EDGE,"E46.MirrorCS"),sQuery(id+"F4.wireOp",EDGE,"E47.MirrorCS"),sQuery(id+"F4.wireOp",EDGE,"E48.MirrorCS"),subQ3,sQuery(id+"F4.wireOp",EDGE,"E51")])],"isStart":false})})],"blendedInto":[makeQuery(id+"F8.boolean.opBoolean","SPLIT",FACE,{"disambiguationData":[TD([makeQuery(id+"F5.opExtrude","SWEPT_FACE",FACE,{"disambiguationData":[OSD([subQ5])]})])],"derivedFrom":makeQuery(id+"F5.opExtrude","CAP_FACE",FACE,{"disambiguationData":[OSD([subQ5,subQ4,subQ6,sQuery(id+"F4.wireOp",EDGE,"E36"),sQuery(id+"F4.wireOp",EDGE,"E37"),sQuery(id+"F4.wireOp",EDGE,"E44.MirrorCS"),sQuery(id+"F4.wireOp",EDGE,"E45.MirrorCS"),sQuery(id+"F4.wireOp",EDGE,"E46.MirrorCS"),sQuery(id+"F4.wireOp",EDGE,"E47.MirrorCS"),sQuery(id+"F4.wireOp",EDGE,"E48.MirrorCS"),subQ3,sQuery(id+"F4.wireOp",EDGE,"E51")])],"isStart":false})})]}),makeQuery(id+"F12.boolean.opBoolean","MERGE",FACE,{"derivedFrom":[makeQuery(id+"F8.boolean.opBoolean","MERGE",FACE,{"derivedFrom":[subQ2,subQ1]}),makeQuery(id+"F12.opExtrude","SWEPT_FACE",FACE,{"disambiguationData":[OSD([sQuery(id+"F11.wireOp",EDGE,"E72.0")])]})]})],"blendedInto":[makeQuery(id+"F12.boolean.opBoolean","MERGE",FACE,{"derivedFrom":[makeQuery(id+"F8.boolean.opBoolean","MERGE",FACE,{"derivedFrom":[subQ2,subQ1]}),makeQuery(id+"F12.opExtrude","SWEPT_FACE",FACE,{"disambiguationData":[OSD([sQuery(id+"F11.wireOp",EDGE,"E72.0")])]})]})]});}
            var Q6;
            Q6=makeQuery(id+"F8.boolean.opBoolean","INTERSECT",EDGE,{"disambiguationData":[OD(1.0)],"derivedFrom":[makeQuery(id+"F5.opExtrude","CAP_FACE",FACE,{"disambiguationData":[OSD([sQuery(id+"F4.wireOp",EDGE,"E33"),sQuery(id+"F4.wireOp",EDGE,"E34"),sQuery(id+"F4.wireOp",EDGE,"E35"),sQuery(id+"F4.wireOp",EDGE,"E36"),sQuery(id+"F4.wireOp",EDGE,"E37"),sQuery(id+"F4.wireOp",EDGE,"E44.MirrorCS"),sQuery(id+"F4.wireOp",EDGE,"E45.MirrorCS"),sQuery(id+"F4.wireOp",EDGE,"E46.MirrorCS"),sQuery(id+"F4.wireOp",EDGE,"E47.MirrorCS"),sQuery(id+"F4.wireOp",EDGE,"E48.MirrorCS"),sQuery(id+"F4.wireOp",EDGE,"E50"),sQuery(id+"F4.wireOp",EDGE,"E51")])],"isStart":false}),makeQuery(id+"F8.opExtrude","SWEPT_FACE",FACE,{"disambiguationData":[OSD([sQuery(id+"F6.wireOp",EDGE,"E64")])]})]});
            var Q7;
            {var subQ0=sQuery(id+"F6.wireOp",EDGE,"E64");var subQ1=makeQuery(id+"F8.opExtrude","SWEPT_FACE",FACE,{"disambiguationData":[OSD([subQ0])]});var subQ2=makeQuery(id+"F7.opExtrude","SWEPT_FACE",FACE,{"disambiguationData":[OSD([subQ0])]});var subQ3=sQuery(id+"F4.wireOp",EDGE,"E51");var subQ4=sQuery(id+"F4.wireOp",EDGE,"E45.MirrorCS");var subQ5=sQuery(id+"F4.wireOp",EDGE,"E44.MirrorCS");var subQ6=sQuery(id+"F4.wireOp",EDGE,"E46.MirrorCS");Q7=makeQuery(id+"F13.opFillet","BLEND_EDGE",EDGE,{"blendedFrom":[makeQuery(id+"F9.opFillet","BLEND_EDGE",EDGE,{"blendedFrom":[makeQuery(id+"F5.opExtrude","SWEPT_EDGE",EDGE,{"disambiguationData":[OSD([subQ4,subQ6])]}),makeQuery(id+"F8.boolean.opBoolean","SPLIT",FACE,{"disambiguationData":[TD([makeQuery(id+"F5.opExtrude","SWEPT_FACE",FACE,{"disambiguationData":[OSD([subQ5])]})])],"derivedFrom":makeQuery(id+"F5.opExtrude","CAP_FACE",FACE,{"disambiguationData":[OSD([sQuery(id+"F4.wireOp",EDGE,"E33"),sQuery(id+"F4.wireOp",EDGE,"E34"),sQuery(id+"F4.wireOp",EDGE,"E35"),sQuery(id+"F4.wireOp",EDGE,"E36"),sQuery(id+"F4.wireOp",EDGE,"E37"),subQ5,subQ4,subQ6,sQuery(id+"F4.wireOp",EDGE,"E47.MirrorCS"),sQuery(id+"F4.wireOp",EDGE,"E48.MirrorCS"),sQuery(id+"F4.wireOp",EDGE,"E50"),subQ3])],"isStart":false})})],"blendedInto":[makeQuery(id+"F8.boolean.opBoolean","SPLIT",FACE,{"disambiguationData":[TD([makeQuery(id+"F5.opExtrude","SWEPT_FACE",FACE,{"disambiguationData":[OSD([subQ5])]})])],"derivedFrom":makeQuery(id+"F5.opExtrude","CAP_FACE",FACE,{"disambiguationData":[OSD([sQuery(id+"F4.wireOp",EDGE,"E33"),sQuery(id+"F4.wireOp",EDGE,"E34"),sQuery(id+"F4.wireOp",EDGE,"E35"),sQuery(id+"F4.wireOp",EDGE,"E36"),sQuery(id+"F4.wireOp",EDGE,"E37"),subQ5,subQ4,subQ6,sQuery(id+"F4.wireOp",EDGE,"E47.MirrorCS"),sQuery(id+"F4.wireOp",EDGE,"E48.MirrorCS"),sQuery(id+"F4.wireOp",EDGE,"E50"),subQ3])],"isStart":false})})]}),makeQuery(id+"F12.boolean.opBoolean","MERGE",FACE,{"derivedFrom":[makeQuery(id+"F8.boolean.opBoolean","MERGE",FACE,{"derivedFrom":[subQ2,subQ1]}),makeQuery(id+"F12.opExtrude","SWEPT_FACE",FACE,{"disambiguationData":[OSD([sQuery(id+"F11.wireOp",EDGE,"E72.0")])]})]})],"blendedInto":[makeQuery(id+"F12.boolean.opBoolean","MERGE",FACE,{"derivedFrom":[makeQuery(id+"F8.boolean.opBoolean","MERGE",FACE,{"derivedFrom":[subQ2,subQ1]}),makeQuery(id+"F12.opExtrude","SWEPT_FACE",FACE,{"disambiguationData":[OSD([sQuery(id+"F11.wireOp",EDGE,"E72.0")])]})]})]});}
            var Q8;
            Q8=makeQuery(id+"F8.boolean.opBoolean","INTERSECT",EDGE,{"disambiguationData":[OD(0.0)],"derivedFrom":[makeQuery(id+"F5.opExtrude","CAP_FACE",FACE,{"disambiguationData":[OSD([sQuery(id+"F4.wireOp",EDGE,"E33"),sQuery(id+"F4.wireOp",EDGE,"E34"),sQuery(id+"F4.wireOp",EDGE,"E35"),sQuery(id+"F4.wireOp",EDGE,"E36"),sQuery(id+"F4.wireOp",EDGE,"E37"),sQuery(id+"F4.wireOp",EDGE,"E44.MirrorCS"),sQuery(id+"F4.wireOp",EDGE,"E45.MirrorCS"),sQuery(id+"F4.wireOp",EDGE,"E46.MirrorCS"),sQuery(id+"F4.wireOp",EDGE,"E47.MirrorCS"),sQuery(id+"F4.wireOp",EDGE,"E48.MirrorCS"),sQuery(id+"F4.wireOp",EDGE,"E50"),sQuery(id+"F4.wireOp",EDGE,"E51")])],"isStart":false}),makeQuery(id+"F8.opExtrude","SWEPT_FACE",FACE,{"disambiguationData":[OSD([sQuery(id+"F6.wireOp",EDGE,"E64")])]})]});
            var Q9;
            {var subQ0=sQuery(id+"F6.wireOp",EDGE,"E64");var subQ1=makeQuery(id+"F8.opExtrude","SWEPT_FACE",FACE,{"disambiguationData":[OSD([subQ0])]});var subQ2=makeQuery(id+"F7.opExtrude","SWEPT_FACE",FACE,{"disambiguationData":[OSD([subQ0])]});var subQ3=sQuery(id+"F4.wireOp",EDGE,"E51");var subQ4=sQuery(id+"F4.wireOp",EDGE,"E37");var subQ5=sQuery(id+"F4.wireOp",EDGE,"E36");var subQ6=sQuery(id+"F4.wireOp",EDGE,"E35");Q9=makeQuery(id+"F13.opFillet","BLEND_EDGE",EDGE,{"blendedFrom":[makeQuery(id+"F9.opFillet","BLEND_EDGE",EDGE,{"blendedFrom":[makeQuery(id+"F5.opExtrude","SWEPT_EDGE",EDGE,{"disambiguationData":[OSD([subQ6,subQ5])]}),makeQuery(id+"F8.boolean.opBoolean","SPLIT",FACE,{"disambiguationData":[TD([makeQuery(id+"F5.opExtrude","SWEPT_FACE",FACE,{"disambiguationData":[OSD([subQ5])]})])],"derivedFrom":makeQuery(id+"F5.opExtrude","CAP_FACE",FACE,{"disambiguationData":[OSD([sQuery(id+"F4.wireOp",EDGE,"E33"),sQuery(id+"F4.wireOp",EDGE,"E34"),subQ6,subQ5,subQ4,sQuery(id+"F4.wireOp",EDGE,"E44.MirrorCS"),sQuery(id+"F4.wireOp",EDGE,"E45.MirrorCS"),sQuery(id+"F4.wireOp",EDGE,"E46.MirrorCS"),sQuery(id+"F4.wireOp",EDGE,"E47.MirrorCS"),sQuery(id+"F4.wireOp",EDGE,"E48.MirrorCS"),sQuery(id+"F4.wireOp",EDGE,"E50"),subQ3])],"isStart":false})})],"blendedInto":[makeQuery(id+"F8.boolean.opBoolean","SPLIT",FACE,{"disambiguationData":[TD([makeQuery(id+"F5.opExtrude","SWEPT_FACE",FACE,{"disambiguationData":[OSD([subQ5])]})])],"derivedFrom":makeQuery(id+"F5.opExtrude","CAP_FACE",FACE,{"disambiguationData":[OSD([sQuery(id+"F4.wireOp",EDGE,"E33"),sQuery(id+"F4.wireOp",EDGE,"E34"),subQ6,subQ5,subQ4,sQuery(id+"F4.wireOp",EDGE,"E44.MirrorCS"),sQuery(id+"F4.wireOp",EDGE,"E45.MirrorCS"),sQuery(id+"F4.wireOp",EDGE,"E46.MirrorCS"),sQuery(id+"F4.wireOp",EDGE,"E47.MirrorCS"),sQuery(id+"F4.wireOp",EDGE,"E48.MirrorCS"),sQuery(id+"F4.wireOp",EDGE,"E50"),subQ3])],"isStart":false})})]}),makeQuery(id+"F12.boolean.opBoolean","MERGE",FACE,{"derivedFrom":[makeQuery(id+"F8.boolean.opBoolean","MERGE",FACE,{"derivedFrom":[subQ2,subQ1]}),makeQuery(id+"F12.opExtrude","SWEPT_FACE",FACE,{"disambiguationData":[OSD([sQuery(id+"F11.wireOp",EDGE,"E72.0")])]})]})],"blendedInto":[makeQuery(id+"F12.boolean.opBoolean","MERGE",FACE,{"derivedFrom":[makeQuery(id+"F8.boolean.opBoolean","MERGE",FACE,{"derivedFrom":[subQ2,subQ1]}),makeQuery(id+"F12.opExtrude","SWEPT_FACE",FACE,{"disambiguationData":[OSD([sQuery(id+"F11.wireOp",EDGE,"E72.0")])]})]})]});}
            fillet(context, id + "F14", {"entities" : qUnion([Q0, Q1, Q2, Q3, Q4, Q5, Q6, Q7, Q8, Q9]), "radius" : 0.5 * mm, "tangentPropagation" : true, "allowEdgeOverflow" : false});
        }
        {
            var Q0;
            {var subQ1=sQuery(id+"F4.wireOp",EDGE,"E51");var subQ2=sQuery(id+"F4.wireOp",EDGE,"E45.MirrorCS");var subQ3=sQuery(id+"F4.wireOp",EDGE,"E44.MirrorCS");Q0=makeQuery(id+"F8.boolean.opBoolean","SPLIT",FACE,{"disambiguationData":[TD([makeQuery(id+"F5.opExtrude","SWEPT_FACE",FACE,{"disambiguationData":[OSD([subQ3])]})])],"derivedFrom":makeQuery(id+"F5.opExtrude","CAP_FACE",FACE,{"disambiguationData":[OSD([sQuery(id+"F4.wireOp",EDGE,"E33"),sQuery(id+"F4.wireOp",EDGE,"E34"),sQuery(id+"F4.wireOp",EDGE,"E35"),sQuery(id+"F4.wireOp",EDGE,"E36"),sQuery(id+"F4.wireOp",EDGE,"E37"),subQ3,subQ2,sQuery(id+"F4.wireOp",EDGE,"E46.MirrorCS"),sQuery(id+"F4.wireOp",EDGE,"E47.MirrorCS"),sQuery(id+"F4.wireOp",EDGE,"E48.MirrorCS"),sQuery(id+"F4.wireOp",EDGE,"E50"),subQ1])],"isStart":false})});}
            var sketch = newSketch(context, id + "F15", { "sketchPlane" : qUnion([Q0])});
            skLineSegment(sketch, "E74.0.0", {"start": v(117.33, 50.9) * mm, "end": v(115.65, 48) * mm});
            skLineSegment(sketch, "E74.0.1", {"start": v(115.65, 48) * mm, "end": v(117.33, 45.1) * mm});
            skLineSegment(sketch, "E74.0.2", {"start": v(117.33, 45.1) * mm, "end": v(120.67, 45.1) * mm});
            skLineSegment(sketch, "E74.0.3", {"start": v(120.67, 45.1) * mm, "end": v(122.35, 48) * mm});
            skLineSegment(sketch, "E74.0.4", {"start": v(122.35, 48) * mm, "end": v(120.67, 50.9) * mm});
            skLineSegment(sketch, "E74.0.5", {"start": v(120.67, 50.9) * mm, "end": v(117.33, 50.9) * mm});
            skLineSegment(sketch, "E75.0.0", {"start": v(141.33, 50.9) * mm, "end": v(139.65, 48) * mm});
            skLineSegment(sketch, "E75.0.1", {"start": v(139.65, 48) * mm, "end": v(141.33, 45.1) * mm});
            skLineSegment(sketch, "E75.0.2", {"start": v(141.33, 45.1) * mm, "end": v(144.67, 45.1) * mm});
            skLineSegment(sketch, "E75.0.3", {"start": v(144.67, 45.1) * mm, "end": v(146.35, 48) * mm});
            skLineSegment(sketch, "E75.0.4", {"start": v(146.35, 48) * mm, "end": v(144.67, 50.9) * mm});
            skLineSegment(sketch, "E75.0.5", {"start": v(144.67, 50.9) * mm, "end": v(141.33, 50.9) * mm});
            skLineSegment(sketch, "E76.0.0", {"start": v(144.67, 89.1) * mm, "end": v(146.35, 92) * mm});
            skLineSegment(sketch, "E76.0.1", {"start": v(146.35, 92) * mm, "end": v(144.67, 94.9) * mm});
            skLineSegment(sketch, "E76.0.2", {"start": v(144.67, 94.9) * mm, "end": v(141.33, 94.9) * mm});
            skLineSegment(sketch, "E76.0.3", {"start": v(141.33, 94.9) * mm, "end": v(139.65, 92) * mm});
            skLineSegment(sketch, "E76.0.4", {"start": v(139.65, 92) * mm, "end": v(141.33, 89.1) * mm});
            skLineSegment(sketch, "E76.0.5", {"start": v(141.33, 89.1) * mm, "end": v(144.67, 89.1) * mm});
            skLineSegment(sketch, "E76.1.0", {"start": v(120.67, 89.1) * mm, "end": v(122.35, 92) * mm});
            skLineSegment(sketch, "E76.1.1", {"start": v(122.35, 92) * mm, "end": v(120.67, 94.9) * mm});
            skLineSegment(sketch, "E76.1.2", {"start": v(120.67, 94.9) * mm, "end": v(117.33, 94.9) * mm});
            skLineSegment(sketch, "E76.1.3", {"start": v(117.33, 94.9) * mm, "end": v(115.65, 92) * mm});
            skLineSegment(sketch, "E76.1.4", {"start": v(115.65, 92) * mm, "end": v(117.33, 89.1) * mm});
            skLineSegment(sketch, "E76.1.5", {"start": v(117.33, 89.1) * mm, "end": v(120.67, 89.1) * mm});
            skLineSegment(sketch, "E77.0.0", {"start": v(-2.1, 71.67) * mm, "end": v(-5, 73.35) * mm});
            skLineSegment(sketch, "E77.0.1", {"start": v(-5, 73.35) * mm, "end": v(-7.9, 71.67) * mm});
            skLineSegment(sketch, "E77.0.2", {"start": v(-7.9, 71.67) * mm, "end": v(-7.9, 68.33) * mm});
            skLineSegment(sketch, "E77.0.3", {"start": v(-7.9, 68.33) * mm, "end": v(-5, 66.65) * mm});
            skLineSegment(sketch, "E77.0.4", {"start": v(-5, 66.65) * mm, "end": v(-2.1, 68.33) * mm});
            skLineSegment(sketch, "E77.0.5", {"start": v(-2.1, 68.33) * mm, "end": v(-2.1, 71.67) * mm});
            skLineSegment(sketch, "E77.1.0", {"start": v(17.33, 50.9) * mm, "end": v(15.65, 48) * mm});
            skLineSegment(sketch, "E77.1.1", {"start": v(15.65, 48) * mm, "end": v(17.33, 45.1) * mm});
            skLineSegment(sketch, "E77.1.2", {"start": v(17.33, 45.1) * mm, "end": v(20.67, 45.1) * mm});
            skLineSegment(sketch, "E77.1.3", {"start": v(20.67, 45.1) * mm, "end": v(22.35, 48) * mm});
            skLineSegment(sketch, "E77.1.4", {"start": v(22.35, 48) * mm, "end": v(20.67, 50.9) * mm});
            skLineSegment(sketch, "E77.1.5", {"start": v(20.67, 50.9) * mm, "end": v(17.33, 50.9) * mm});
            skLineSegment(sketch, "E77.2.0", {"start": v(20.67, 89.1) * mm, "end": v(22.35, 92) * mm});
            skLineSegment(sketch, "E77.2.1", {"start": v(22.35, 92) * mm, "end": v(20.67, 94.9) * mm});
            skLineSegment(sketch, "E77.2.2", {"start": v(20.67, 94.9) * mm, "end": v(17.33, 94.9) * mm});
            skLineSegment(sketch, "E77.2.3", {"start": v(17.33, 94.9) * mm, "end": v(15.65, 92) * mm});
            skLineSegment(sketch, "E77.2.4", {"start": v(15.65, 92) * mm, "end": v(17.33, 89.1) * mm});
            skLineSegment(sketch, "E77.2.5", {"start": v(17.33, 89.1) * mm, "end": v(20.67, 89.1) * mm});
            skSolve(sketch);
        }
        {
            var Q0;
            Q0=makeQuery(id+"F15.imprint","IMPRINT",FACE,{"disambiguationData":[TD([[makeQuery(id+"F15.imprint","IMPRINT",EDGE,{"derivedFrom":sQuery(id+"F15.wireOp",EDGE,"E74.0.0")}),1.0]])]});
            var Q1;
            Q1=makeQuery(id+"F15.imprint","IMPRINT",FACE,{"disambiguationData":[TD([[makeQuery(id+"F15.imprint","IMPRINT",EDGE,{"derivedFrom":sQuery(id+"F15.wireOp",EDGE,"E75.0.0")}),1.0]])]});
            var Q2;
            Q2=makeQuery(id+"F15.imprint","IMPRINT",FACE,{"disambiguationData":[TD([[makeQuery(id+"F15.imprint","IMPRINT",EDGE,{"derivedFrom":sQuery(id+"F15.wireOp",EDGE,"E76.0.0")}),1.0]])]});
            var Q3;
            Q3=makeQuery(id+"F15.imprint","IMPRINT",FACE,{"disambiguationData":[TD([[makeQuery(id+"F15.imprint","IMPRINT",EDGE,{"derivedFrom":sQuery(id+"F15.wireOp",EDGE,"E76.1.0")}),1.0]])]});
            var Q4;
            Q4=makeQuery(id+"F15.imprint","IMPRINT",FACE,{"disambiguationData":[TD([[makeQuery(id+"F15.imprint","IMPRINT",EDGE,{"derivedFrom":sQuery(id+"F15.wireOp",EDGE,"E77.1.0")}),1.0]])]});
            var Q5;
            Q5=makeQuery(id+"F15.imprint","IMPRINT",FACE,{"disambiguationData":[TD([[makeQuery(id+"F15.imprint","IMPRINT",EDGE,{"derivedFrom":sQuery(id+"F15.wireOp",EDGE,"E77.0.0")}),1.0]])]});
            var Q6;
            Q6=makeQuery(id+"F15.imprint","IMPRINT",FACE,{"disambiguationData":[TD([[makeQuery(id+"F15.imprint","IMPRINT",EDGE,{"derivedFrom":sQuery(id+"F15.wireOp",EDGE,"E77.2.0")}),1.0]])]});
            extrude(context, id + "F16", {"entities" : qUnion([Q0, Q1, Q2, Q3, Q4, Q5, Q6]), "operationType" : NewBodyOperationType.REMOVE, "oppositeDirection" : true, "depth" : 2.5 * mm});
        }
        {
            var Q0;
            {var subQ0=sQuery(id+"F4.wireOp",EDGE,"E55");Q0=makeQuery(id+"F13.opFillet","BLEND_EDGE",EDGE,{"blendedFrom":[makeQuery(id+"F5.opExtrude","CAP_EDGE",EDGE,{"disambiguationData":[OSD([subQ0])],"isStart":false}),makeQuery(id+"F5.opExtrude","CAP_FACE",FACE,{"disambiguationData":[OSD([sQuery(id+"F4.wireOp",EDGE,"E52"),sQuery(id+"F4.wireOp",EDGE,"E53"),sQuery(id+"F4.wireOp",EDGE,"E54"),subQ0,sQuery(id+"F4.wireOp",EDGE,"E56"),sQuery(id+"F4.wireOp",EDGE,"E57"),sQuery(id+"F4.wireOp",EDGE,"E58"),sQuery(id+"F4.wireOp",EDGE,"E59"),sQuery(id+"F4.wireOp",EDGE,"E60"),sQuery(id+"F4.wireOp",EDGE,"E61"),sQuery(id+"F4.wireOp",EDGE,"E62"),sQuery(id+"F4.wireOp",EDGE,"E63")])],"isStart":false})],"blendedInto":[makeQuery(id+"F5.opExtrude","CAP_FACE",FACE,{"disambiguationData":[OSD([sQuery(id+"F4.wireOp",EDGE,"E52"),sQuery(id+"F4.wireOp",EDGE,"E53"),sQuery(id+"F4.wireOp",EDGE,"E54"),subQ0,sQuery(id+"F4.wireOp",EDGE,"E56"),sQuery(id+"F4.wireOp",EDGE,"E57"),sQuery(id+"F4.wireOp",EDGE,"E58"),sQuery(id+"F4.wireOp",EDGE,"E59"),sQuery(id+"F4.wireOp",EDGE,"E60"),sQuery(id+"F4.wireOp",EDGE,"E61"),sQuery(id+"F4.wireOp",EDGE,"E62"),sQuery(id+"F4.wireOp",EDGE,"E63")])],"isStart":false})]});}
            cPoint(context, id + "F17", {"entities" : qUnion([Q0]), "parameter" : 0.5});
        }
        {
            var Q0;
            Q0=qCreatedBy(makeId("Front.planeOp"),FACE);
            var Q1;
            Q1=qCreatedBy(id+"F17",VERTEX);
            cPlane(context, id + "F18", {"entities" : qUnion([Q0, Q1]), "cplaneType" : CPlaneType.PLANE_POINT, "offset" : 25 * mm, "width" : 150 * mm, "height" : 150 * mm});
        }
        {
            var Q0;
            Q0=qCreatedBy(id+"F18.planeOp",FACE);
            var sketch = newSketch(context, id + "F19", { "sketchPlane" : qUnion([Q0])});
            skLineSegment(sketch, "E78.0", {"start": v(1, -13) * mm, "end": v(13, -13) * mm, "construction": true});
            skPoint(sketch, "E79.0", {"position": v(7, -13) * mm});
            skCircle(sketch, "E80", {"center": v(7, -21.05) * mm, "radius": 6.05 * mm});
            skCircle(sketch, "E81.0", {"center": v(7, -21.05) * mm, "radius": 7.95 * mm});
            skLineSegment(sketch, "E82", {"start": v(7, -21.05) * mm, "end": v(7, -13) * mm, "construction": true});
            skLineSegment(sketch, "E83", {"start": v(-0.95, -13) * mm, "end": v(-0.95, -21.05) * mm});
            skLineSegment(sketch, "E84", {"start": v(14.95, -13) * mm, "end": v(14.95, -21.05) * mm});
            skLineSegment(sketch, "E85", {"start": v(-0.95, -13) * mm, "end": v(14.95, -13) * mm});
            skLineSegment(sketch, "E86", {"start": v(7, -21.05) * mm, "end": v(12.62, -26.67) * mm});
            skLineSegment(sketch, "E87.MirrorCS", {"start": v(7, -21.05) * mm, "end": v(1.38, -26.67) * mm});
            skSolve(sketch);
        }
        {
            var Q0;
            {var subQ5=sQuery(id+"F19.wireOp",EDGE,"E80");var subQ8=sQuery(id+"F19.wireOp",EDGE,"E86");var subQ9=makeQuery(id+"F19.imprint","INTERSECT",VERTEX,{"derivedFrom":[subQ5,subQ8]});Q0=makeQuery(id+"F19.imprint","IMPRINT",FACE,{"disambiguationData":[TD([[makeQuery(id+"F19.imprint","IMPRINT",EDGE,{"disambiguationData":[TD([[subQ9,-1.0]])],"derivedFrom":subQ5}),-1.0]])]});}
            var Q1;
            {var subQ0=sQuery(id+"F19.wireOp",EDGE,"E83");Q1=makeQuery(id+"F19.imprint","IMPRINT",FACE,{"disambiguationData":[TD([[makeQuery(id+"F19.imprint","IMPRINT",EDGE,{"derivedFrom":subQ0}),1.0]])]});}
            var Q2;
            {var subQ0=sQuery(id+"F19.wireOp",EDGE,"E84");Q2=makeQuery(id+"F19.imprint","IMPRINT",FACE,{"disambiguationData":[TD([[makeQuery(id+"F19.imprint","IMPRINT",EDGE,{"derivedFrom":subQ0}),-1.0]])]});}
            extrude(context, id + "F20", {"entities" : qUnion([Q0, Q1, Q2]), "operationType" : NewBodyOperationType.ADD, "depth" : 6.75 * mm, "hasSecondDirection" : true, "secondDirectionOppositeDirection" : true, "secondDirectionDepth" : 6.75 * mm});
        }
        {
            var Q0;
            {var subQ0=sQuery(id+"F19.wireOp",EDGE,"E86");var subQ1=sQuery(id+"F19.wireOp",EDGE,"E80");var subQ2=makeQuery(id+"F19.imprint","INTERSECT",VERTEX,{"derivedFrom":[subQ1,subQ0]});Q0=makeQuery(id+"F19.imprint","IMPRINT",FACE,{"disambiguationData":[TD([[makeQuery(id+"F19.imprint","IMPRINT",EDGE,{"disambiguationData":[TD([[subQ2,-1.0]])],"derivedFrom":subQ1}),1.0]])]});}
            extrude(context, id + "F21", {"entities" : qUnion([Q0]), "operationType" : NewBodyOperationType.REMOVE, "endBound" : BoundingType.THROUGH_ALL, "oppositeDirection" : true, "depth" : 25 * mm, "hasSecondDirection" : true, "secondDirectionBound" : SecondDirectionBoundingType.THROUGH_ALL, "secondDirectionOppositeDirection" : false, "secondDirectionDepth" : 25 * mm});
        }
        {
            var Q0;
            {var subQ0=sQuery(id+"F4.wireOp",EDGE,"E50");var subQ1=makeQuery(id+"F5.opExtrude","CAP_EDGE",EDGE,{"disambiguationData":[OSD([subQ0])],"isStart":true});Q0=makeQuery(id+"F12.boolean.opBoolean","MERGE",FACE,{"derivedFrom":[makeQuery(id+"F5.opExtrude","CAP_FACE",FACE,{"disambiguationData":[OSD([sQuery(id+"F4.wireOp",EDGE,"E33"),sQuery(id+"F4.wireOp",EDGE,"E34"),sQuery(id+"F4.wireOp",EDGE,"E35"),sQuery(id+"F4.wireOp",EDGE,"E36"),sQuery(id+"F4.wireOp",EDGE,"E37"),sQuery(id+"F4.wireOp",EDGE,"E44.MirrorCS"),sQuery(id+"F4.wireOp",EDGE,"E45.MirrorCS"),sQuery(id+"F4.wireOp",EDGE,"E46.MirrorCS"),sQuery(id+"F4.wireOp",EDGE,"E47.MirrorCS"),sQuery(id+"F4.wireOp",EDGE,"E48.MirrorCS"),subQ0,sQuery(id+"F4.wireOp",EDGE,"E51")])],"isStart":true}),makeQuery(id+"F12.opExtrude","SWEPT_FACE",FACE,{"disambiguationData":[OSD([subQ0]),TDD([makeQuery(id+"F11.imprint","IMPRINT",EDGE,{"disambiguationData":[TD([[makeQuery(id+"F11.imprint","INTERSECT",VERTEX,{"derivedFrom":[subQ1,sQuery(id+"F11.wireOp",EDGE,"E73.2")]}),-1.0]])],"derivedFrom":subQ1})])]})]});}
            var sketch = newSketch(context, id + "F22", { "sketchPlane" : qUnion([Q0])});
            skCircle(sketch, "E88.0", {"center": v(19, -48) * mm, "radius": 1.65 * mm});
            skCircle(sketch, "E88.1", {"center": v(19, -92) * mm, "radius": 1.65 * mm});
            skCircle(sketch, "E88.2", {"center": v(119, -92) * mm, "radius": 1.65 * mm});
            skCircle(sketch, "E88.3", {"center": v(119, -48) * mm, "radius": 1.65 * mm});
            skLineSegment(sketch, "E89.bottom", {"start": v(80.69, -54) * mm, "end": v(52.69, -54) * mm});
            skLineSegment(sketch, "E89.top", {"start": v(80.69, -42) * mm, "end": v(52.69, -42) * mm});
            skLineSegment(sketch, "E89.left", {"start": v(80.69, -54) * mm, "end": v(80.69, -42) * mm});
            skLineSegment(sketch, "E89.right", {"start": v(52.69, -54) * mm, "end": v(52.69, -42) * mm});
            skPoint(sketch, "E89.middle", {"position": v(66.69, -48) * mm});
            skLineSegment(sketch, "E90.bottom", {"start": v(80.69, -86) * mm, "end": v(52.69, -86) * mm});
            skLineSegment(sketch, "E90.top", {"start": v(80.69, -98) * mm, "end": v(52.69, -98) * mm});
            skLineSegment(sketch, "E90.left", {"start": v(80.69, -86) * mm, "end": v(80.69, -98) * mm});
            skLineSegment(sketch, "E90.right", {"start": v(52.69, -86) * mm, "end": v(52.69, -98) * mm});
            skPoint(sketch, "E90.middle", {"position": v(66.69, -92) * mm});
            skPoint(sketch, "E91", {"position": v(58.69, -48) * mm});
            skPoint(sketch, "E92", {"position": v(74.69, -92) * mm});
            skLineSegment(sketch, "E93", {"start": v(66.69, -48) * mm, "end": v(66.69, -92) * mm, "construction": true});
            skPoint(sketch, "E94.MirrorP", {"position": v(58.69, -92) * mm});
            skPoint(sketch, "E95.MirrorP", {"position": v(74.69, -48) * mm});
            skLineSegment(sketch, "E96", {"start": v(74.69, -48) * mm, "end": v(80.69, -48) * mm, "construction": true});
            skLineSegment(sketch, "E97", {"start": v(74.69, -48) * mm, "end": v(74.69, -54) * mm, "construction": true});
            skLineSegment(sketch, "E98.0", {"start": v(20, -42) * mm, "end": v(18, -42) * mm});
            skLineSegment(sketch, "E99.0", {"start": v(25, -51.11) * mm, "end": v(25, -47) * mm});
            skLineSegment(sketch, "E100.bottom", {"start": v(25, -42) * mm, "end": v(13, -42) * mm});
            skLineSegment(sketch, "E100.top", {"start": v(25, -54) * mm, "end": v(13, -54) * mm});
            skLineSegment(sketch, "E100.left", {"start": v(25, -42) * mm, "end": v(25, -54) * mm});
            skLineSegment(sketch, "E100.right", {"start": v(13, -42) * mm, "end": v(13, -54) * mm});
            skFitSpline(sketch, "E101", {"points": [v(25, -42) * mm, v(41.67, -67.17) * mm, v(52.69, -86) * mm], "startDerivative": vector(66.6, 0) * mm, "endDerivative": vector(65.3, 0) * mm});
            skLineSegment(sketch, "E102", {"start": v(25, -42) * mm, "end": v(52.69, -42) * mm, "construction": true});
            skPoint(sketch, "E103", {"position": v(38.84, -42) * mm});
            skCircle(sketch, "E104.0", {"center": v(-5, -70) * mm, "radius": 1.65 * mm});
            skPoint(sketch, "E105.cornerSnap0", {"position": v(113, -49.06) * mm});
            skFitSpline(sketch, "E106", {"points": [v(52.69, -98) * mm, v(36.01, -72.83) * mm, v(25, -54) * mm], "startDerivative": vector(-66.6, 0) * mm, "endDerivative": vector(-65.3, 0) * mm});
            skLineSegment(sketch, "E107", {"start": v(-5, -70) * mm, "end": v(38.84, -70) * mm, "construction": true});
            skLineSegment(sketch, "E108", {"start": v(38.84, -70) * mm, "end": v(38.84, -42) * mm, "construction": true});
            skLineSegment(sketch, "E109", {"start": v(36.01, -72.83) * mm, "end": v(38.84, -70) * mm, "construction": true});
            skLineSegment(sketch, "E110", {"start": v(41.67, -67.17) * mm, "end": v(38.84, -70) * mm, "construction": true});
            skFitSpline(sketch, "E111.MirrorCS", {"points": [v(52.69, -42) * mm, v(36.01, -67.17) * mm, v(25, -86) * mm], "startDerivative": vector(-66.6, 0) * mm, "endDerivative": vector(-65.3, 0) * mm});
            skFitSpline(sketch, "E112.MirrorCS", {"points": [v(25, -98) * mm, v(41.67, -72.83) * mm, v(52.69, -54) * mm], "startDerivative": vector(66.6, 0) * mm, "endDerivative": vector(65.3, 0) * mm});
            skLineSegment(sketch, "E113.MirrorCS", {"start": v(25, -98) * mm, "end": v(13, -98) * mm});
            skLineSegment(sketch, "E114.MirrorCS", {"start": v(13, -98) * mm, "end": v(13, -86) * mm});
            skLineSegment(sketch, "E115.MirrorCS", {"start": v(25, -86) * mm, "end": v(13, -86) * mm});
            skFitSpline(sketch, "E116", {"points": [v(80.69, -42) * mm, v(99.67, -67.17) * mm, v(113, -86) * mm], "startDerivative": vector(66.8, 0) * mm, "endDerivative": vector(65.07, 0) * mm});
            skLineSegment(sketch, "E117.bottom", {"start": v(125, -42) * mm, "end": v(113, -42) * mm});
            skLineSegment(sketch, "E117.top", {"start": v(125, -54) * mm, "end": v(113, -54) * mm});
            skLineSegment(sketch, "E117.left", {"start": v(125, -42) * mm, "end": v(125, -54) * mm});
            skLineSegment(sketch, "E117.right", {"start": v(113, -42) * mm, "end": v(113, -54) * mm});
            skLineSegment(sketch, "E118.MirrorCS", {"start": v(125, -98) * mm, "end": v(113, -98) * mm});
            skLineSegment(sketch, "E119.MirrorCS", {"start": v(113, -98) * mm, "end": v(113, -86) * mm});
            skLineSegment(sketch, "E120.MirrorCS", {"start": v(125, -86) * mm, "end": v(113, -86) * mm});
            skLineSegment(sketch, "E121.MirrorCS", {"start": v(125, -98) * mm, "end": v(125, -86) * mm});
            skFitSpline(sketch, "E122", {"points": [v(80.69, -54) * mm, v(94.01, -72.83) * mm, v(113, -98) * mm], "startDerivative": vector(65.07, 0) * mm, "endDerivative": vector(66.8, 0) * mm});
            skFitSpline(sketch, "E123.MirrorCS", {"points": [v(80.69, -86) * mm, v(94.01, -67.17) * mm, v(113, -42) * mm], "startDerivative": vector(65.07, 0) * mm, "endDerivative": vector(66.8, 0) * mm});
            skFitSpline(sketch, "E124.MirrorCS", {"points": [v(80.69, -98) * mm, v(99.67, -72.83) * mm, v(113, -54) * mm], "startDerivative": vector(66.8, 0) * mm, "endDerivative": vector(65.07, 0) * mm});
            skLineSegment(sketch, "E125", {"start": v(80.69, -42) * mm, "end": v(113, -42) * mm, "construction": true});
            skPoint(sketch, "E126", {"position": v(96.84, -42) * mm});
            skLineSegment(sketch, "E127", {"start": v(96.84, -42) * mm, "end": v(96.84, -70) * mm, "construction": true});
            skLineSegment(sketch, "E128", {"start": v(63.19, -98) * mm, "end": v(63.19, -86) * mm});
            skLineSegment(sketch, "E129", {"start": v(63.19, -54) * mm, "end": v(63.19, -42) * mm});
            skLineSegment(sketch, "E130.MirrorCS", {"start": v(70.19, -98) * mm, "end": v(70.19, -86) * mm});
            skLineSegment(sketch, "E131.MirrorCS", {"start": v(70.19, -54) * mm, "end": v(70.19, -42) * mm});
            skSolve(sketch);
        }
        {
            var Q0;
            Q0=makeQuery(id+"F22.imprint","IMPRINT",FACE,{"disambiguationData":[TD([[makeQuery(id+"F22.imprint","IMPRINT",EDGE,{"derivedFrom":sQuery(id+"F22.wireOp",EDGE,"E88.1")}),-1.0]])]});
            var Q1;
            {var subQ1=sQuery(id+"F22.wireOp",EDGE,"E100.left");var subQ9=makeQuery(id+"F22.imprint","IMPRINT",VERTEX,{"disambiguationData":[OD(0.0)],"derivedFrom":subQ1});Q1=makeQuery(id+"F22.imprint","IMPRINT",FACE,{"disambiguationData":[TD([[makeQuery(id+"F22.imprint","IMPRINT",EDGE,{"disambiguationData":[TD([[subQ9,-1.0]])],"derivedFrom":subQ1}),1.0]])]});}
            var Q2;
            {var subQ0=sQuery(id+"F22.wireOp",EDGE,"E111.MirrorCS");var subQ1=sQuery(id+"F22.wireOp",EDGE,"E101");var subQ2=makeQuery(id+"F22.imprint","INTERSECT",VERTEX,{"derivedFrom":[subQ1,subQ0]});Q2=makeQuery(id+"F22.imprint","IMPRINT",FACE,{"disambiguationData":[TD([[makeQuery(id+"F22.imprint","IMPRINT",EDGE,{"disambiguationData":[TD([[subQ2,-1.0]])],"derivedFrom":subQ1}),-1.0]])]});}
            var Q3;
            {var subQ0=sQuery(id+"F22.wireOp",EDGE,"E89.right");Q3=makeQuery(id+"F22.imprint","IMPRINT",FACE,{"disambiguationData":[TD([[makeQuery(id+"F22.imprint","IMPRINT",EDGE,{"derivedFrom":subQ0}),1.0]])]});}
            var Q4;
            {var subQ0=sQuery(id+"F22.wireOp",EDGE,"E90.right");Q4=makeQuery(id+"F22.imprint","IMPRINT",FACE,{"disambiguationData":[TD([[makeQuery(id+"F22.imprint","IMPRINT",EDGE,{"derivedFrom":subQ0}),-1.0]])]});}
            var Q5;
            Q5=makeQuery(id+"F22.imprint","IMPRINT",FACE,{"disambiguationData":[TD([[makeQuery(id+"F22.imprint","IMPRINT",EDGE,{"derivedFrom":sQuery(id+"F22.wireOp",EDGE,"E89.bottom")}),-1.0]])]});
            var Q6;
            Q6=makeQuery(id+"F22.imprint","IMPRINT",FACE,{"disambiguationData":[TD([[makeQuery(id+"F22.imprint","IMPRINT",EDGE,{"derivedFrom":sQuery(id+"F22.wireOp",EDGE,"E90.bottom")}),1.0]])]});
            var Q7;
            {var subQ0=sQuery(id+"F22.wireOp",EDGE,"E89.left");Q7=makeQuery(id+"F22.imprint","IMPRINT",FACE,{"disambiguationData":[TD([[makeQuery(id+"F22.imprint","IMPRINT",EDGE,{"derivedFrom":subQ0}),-1.0]])]});}
            var Q8;
            {var subQ0=sQuery(id+"F22.wireOp",EDGE,"c6c803b5-7baf-4ce3-ba59-0cdf4308a98c0.MirrorCS");var subQ1=sQuery(id+"F22.wireOp",EDGE,"cb72a9e3-eb21-4311-815f-be3bdb3244270.MirrorCS");var subQ2=makeQuery(id+"F22.imprint","INTERSECT",VERTEX,{"derivedFrom":[subQ1,subQ0]});Q8=makeQuery(id+"F22.imprint","IMPRINT",FACE,{"disambiguationData":[TD([[makeQuery(id+"F22.imprint","IMPRINT",EDGE,{"disambiguationData":[TD([[subQ2,-1.0]])],"derivedFrom":subQ1}),1.0]])]});}
            var Q9;
            {var subQ0=sQuery(id+"F22.wireOp",EDGE,"cb72a9e3-eb21-4311-815f-be3bdb3244270.MirrorCS");var subQ3=sQuery(id+"F22.wireOp",EDGE,"c6c803b5-7baf-4ce3-ba59-0cdf4308a98c0.MirrorCS");var subQ4=makeQuery(id+"F22.imprint","INTERSECT",VERTEX,{"derivedFrom":[subQ0,subQ3]});Q9=makeQuery(id+"F22.imprint","IMPRINT",FACE,{"disambiguationData":[TD([[makeQuery(id+"F22.imprint","IMPRINT",EDGE,{"disambiguationData":[TD([[subQ4,-1.0]])],"derivedFrom":subQ3}),1.0]])]});}
            var Q10;
            Q10=makeQuery(id+"F22.imprint","IMPRINT",FACE,{"disambiguationData":[TD([[makeQuery(id+"F22.imprint","IMPRINT",EDGE,{"derivedFrom":sQuery(id+"F22.wireOp",EDGE,"E88.3")}),-1.0]])]});
            var Q11;
            {var subQ3=sQuery(id+"F4.wireOp",EDGE,"E47.MirrorCS");var subQ16=makeQuery(id+"F5.opExtrude","CAP_EDGE",EDGE,{"disambiguationData":[OSD([subQ3])],"isStart":true});Q11=makeQuery(id+"F22.imprint","IMPRINT",FACE,{"disambiguationData":[TD([[makeQuery(id+"F22.imprint","IMPRINT",EDGE,{"derivedFrom":subQ16}),1.0]])]});}
            var Q12;
            {var subQ0=sQuery(id+"F22.wireOp",EDGE,"E90.left");Q12=makeQuery(id+"F22.imprint","IMPRINT",FACE,{"disambiguationData":[TD([[makeQuery(id+"F22.imprint","IMPRINT",EDGE,{"derivedFrom":subQ0}),1.0]])]});}
            var Q13;
            Q13=makeQuery(id+"F22.imprint","IMPRINT",FACE,{"disambiguationData":[TD([[makeQuery(id+"F22.imprint","IMPRINT",EDGE,{"derivedFrom":sQuery(id+"F22.wireOp",EDGE,"E88.2")}),-1.0]])]});
            var Q14;
            {var subQ0=sQuery(id+"F22.wireOp",EDGE,"E105.left");var subQ1=sQuery(id+"F22.wireOp",EDGE,"E105.top");var subQ2=makeQuery(id+"F22.imprint","INTERSECT",VERTEX,{"derivedFrom":[subQ1,subQ0,sQuery(id+"F22.wireOp",EDGE,"f323a4a8-d413-46e9-a5bd-dff2649972150.MirrorCS")]});Q14=makeQuery(id+"F22.imprint","IMPRINT",FACE,{"disambiguationData":[TD([[makeQuery(id+"F22.imprint","IMPRINT",EDGE,{"disambiguationData":[TD([[subQ2,-1.0]])],"derivedFrom":subQ1}),1.0]])]});}
            var Q15;
            {var subQ1=sQuery(id+"F4.wireOp",EDGE,"E51");var subQ2=sQuery(id+"F4.wireOp",EDGE,"E44.MirrorCS");var subQ3=makeQuery(id+"F9.opFillet","BLEND_EDGE",EDGE,{"blendedFrom":[makeQuery(id+"F5.opExtrude","SWEPT_EDGE",EDGE,{"disambiguationData":[OSD([subQ2,subQ1])]}),makeQuery(id+"F5.opExtrude","CAP_FACE",FACE,{"disambiguationData":[OSD([sQuery(id+"F4.wireOp",EDGE,"E33"),sQuery(id+"F4.wireOp",EDGE,"E34"),sQuery(id+"F4.wireOp",EDGE,"E35"),sQuery(id+"F4.wireOp",EDGE,"E36"),sQuery(id+"F4.wireOp",EDGE,"E37"),subQ2,sQuery(id+"F4.wireOp",EDGE,"E45.MirrorCS"),sQuery(id+"F4.wireOp",EDGE,"E46.MirrorCS"),sQuery(id+"F4.wireOp",EDGE,"E47.MirrorCS"),sQuery(id+"F4.wireOp",EDGE,"E48.MirrorCS"),sQuery(id+"F4.wireOp",EDGE,"E50"),subQ1])],"isStart":true})],"blendedInto":[makeQuery(id+"F5.opExtrude","CAP_FACE",FACE,{"disambiguationData":[OSD([sQuery(id+"F4.wireOp",EDGE,"E33"),sQuery(id+"F4.wireOp",EDGE,"E34"),sQuery(id+"F4.wireOp",EDGE,"E35"),sQuery(id+"F4.wireOp",EDGE,"E36"),sQuery(id+"F4.wireOp",EDGE,"E37"),subQ2,sQuery(id+"F4.wireOp",EDGE,"E45.MirrorCS"),sQuery(id+"F4.wireOp",EDGE,"E46.MirrorCS"),sQuery(id+"F4.wireOp",EDGE,"E47.MirrorCS"),sQuery(id+"F4.wireOp",EDGE,"E48.MirrorCS"),sQuery(id+"F4.wireOp",EDGE,"E50"),subQ1])],"isStart":true})]});Q15=makeQuery(id+"F22.imprint","IMPRINT",FACE,{"disambiguationData":[TD([[makeQuery(id+"F22.imprint","IMPRINT",EDGE,{"derivedFrom":subQ3}),-1.0]])]});}
            var Q16;
            Q16=makeQuery(id+"F22.imprint","IMPRINT",FACE,{"disambiguationData":[TD([[makeQuery(id+"F22.imprint","IMPRINT",EDGE,{"derivedFrom":sQuery(id+"F22.wireOp",EDGE,"E88.0")}),-1.0]])]});
            var Q17;
            {var subQ0=sQuery(id+"F22.wireOp",EDGE,"E123.MirrorCS");var subQ1=sQuery(id+"F22.wireOp",EDGE,"E116");var subQ2=makeQuery(id+"F22.imprint","INTERSECT",VERTEX,{"derivedFrom":[subQ1,subQ0]});Q17=makeQuery(id+"F22.imprint","IMPRINT",FACE,{"disambiguationData":[TD([[makeQuery(id+"F22.imprint","IMPRINT",EDGE,{"disambiguationData":[TD([[subQ2,-1.0]])],"derivedFrom":subQ1}),-1.0]])]});}
            var Q18;
            {var subQ7=sQuery(id+"F22.wireOp",EDGE,"E123.MirrorCS");var subQ11=sQuery(id+"F22.wireOp",EDGE,"E116");var subQ12=makeQuery(id+"F22.imprint","INTERSECT",VERTEX,{"derivedFrom":[subQ11,subQ7]});Q18=makeQuery(id+"F22.imprint","IMPRINT",FACE,{"disambiguationData":[TD([[makeQuery(id+"F22.imprint","IMPRINT",EDGE,{"disambiguationData":[TD([[subQ12,-1.0]])],"derivedFrom":subQ11}),1.0]])]});}
            var Q19;
            {var subQ8=sQuery(id+"F22.wireOp",EDGE,"E122");var subQ12=sQuery(id+"F22.wireOp",EDGE,"E124.MirrorCS");var subQ13=makeQuery(id+"F22.imprint","INTERSECT",VERTEX,{"derivedFrom":[subQ8,subQ12]});Q19=makeQuery(id+"F22.imprint","IMPRINT",FACE,{"disambiguationData":[TD([[makeQuery(id+"F22.imprint","IMPRINT",EDGE,{"disambiguationData":[TD([[subQ13,-1.0]])],"derivedFrom":subQ12}),-1.0]])]});}
            var Q20;
            {var subQ1=sQuery(id+"F4.wireOp",EDGE,"E51");var subQ2=sQuery(id+"F4.wireOp",EDGE,"E50");var subQ3=sQuery(id+"F4.wireOp",EDGE,"E47.MirrorCS");var subQ4=makeQuery(id+"F9.opFillet","BLEND_EDGE",EDGE,{"blendedFrom":[makeQuery(id+"F5.opExtrude","SWEPT_EDGE",EDGE,{"disambiguationData":[OSD([subQ3,subQ2])]}),makeQuery(id+"F7.boolean.opBoolean","MERGE",FACE,{"derivedFrom":[makeQuery(id+"F5.opExtrude","CAP_FACE",FACE,{"disambiguationData":[OSD([sQuery(id+"F4.wireOp",EDGE,"E33"),sQuery(id+"F4.wireOp",EDGE,"E34"),sQuery(id+"F4.wireOp",EDGE,"E35"),sQuery(id+"F4.wireOp",EDGE,"E36"),sQuery(id+"F4.wireOp",EDGE,"E37"),sQuery(id+"F4.wireOp",EDGE,"E44.MirrorCS"),sQuery(id+"F4.wireOp",EDGE,"E45.MirrorCS"),sQuery(id+"F4.wireOp",EDGE,"E46.MirrorCS"),subQ3,sQuery(id+"F4.wireOp",EDGE,"E48.MirrorCS"),subQ2,subQ1])],"isStart":true}),makeQuery(id+"F7.opExtrude","SWEPT_FACE",FACE,{"disambiguationData":[OSD([subQ1])]})]})],"blendedInto":[makeQuery(id+"F7.boolean.opBoolean","MERGE",FACE,{"derivedFrom":[makeQuery(id+"F5.opExtrude","CAP_FACE",FACE,{"disambiguationData":[OSD([sQuery(id+"F4.wireOp",EDGE,"E33"),sQuery(id+"F4.wireOp",EDGE,"E34"),sQuery(id+"F4.wireOp",EDGE,"E35"),sQuery(id+"F4.wireOp",EDGE,"E36"),sQuery(id+"F4.wireOp",EDGE,"E37"),sQuery(id+"F4.wireOp",EDGE,"E44.MirrorCS"),sQuery(id+"F4.wireOp",EDGE,"E45.MirrorCS"),sQuery(id+"F4.wireOp",EDGE,"E46.MirrorCS"),subQ3,sQuery(id+"F4.wireOp",EDGE,"E48.MirrorCS"),subQ2,subQ1])],"isStart":true}),makeQuery(id+"F7.opExtrude","SWEPT_FACE",FACE,{"disambiguationData":[OSD([subQ1])]})]})]});Q20=makeQuery(id+"F22.imprint","IMPRINT",FACE,{"disambiguationData":[TD([[makeQuery(id+"F22.imprint","IMPRINT",EDGE,{"derivedFrom":subQ4}),-1.0]])]});}
            var Q21;
            {var subQ0=sQuery(id+"F22.wireOp",EDGE,"E119.MirrorCS");var subQ6=sQuery(id+"F22.wireOp",EDGE,"E120.MirrorCS");var subQ7=makeQuery(id+"F22.imprint","INTERSECT",VERTEX,{"derivedFrom":[sQuery(id+"F22.wireOp",EDGE,"E116"),subQ0,subQ6]});Q21=makeQuery(id+"F22.imprint","IMPRINT",FACE,{"disambiguationData":[TD([[makeQuery(id+"F22.imprint","IMPRINT",EDGE,{"disambiguationData":[TD([[subQ7,1.0]])],"derivedFrom":subQ0}),-1.0]])]});}
            var Q22;
            {var subQ0=sQuery(id+"F22.wireOp",EDGE,"E117.right");var subQ1=sQuery(id+"F22.wireOp",EDGE,"E117.top");var subQ2=makeQuery(id+"F22.imprint","INTERSECT",VERTEX,{"derivedFrom":[subQ1,subQ0,sQuery(id+"F22.wireOp",EDGE,"E124.MirrorCS")]});Q22=makeQuery(id+"F22.imprint","IMPRINT",FACE,{"disambiguationData":[TD([[makeQuery(id+"F22.imprint","IMPRINT",EDGE,{"disambiguationData":[TD([[subQ2,1.0]])],"derivedFrom":subQ1}),-1.0]])]});}
            extrude(context, id + "F23", {"entities" : qUnion([Q0, Q1, Q2, Q3, Q4, Q5, Q6, Q7, Q8, Q9, Q10, Q11, Q12, Q13, Q14, Q15, Q16, Q17, Q18, Q19, Q20, Q21, Q22]), "depth" : 3 * mm});
        }
        {
            var Q0;
            {var subQ0=sQuery(id+"F22.wireOp",EDGE,"E90.right");Q0=makeQuery(id+"F22.imprint","IMPRINT",FACE,{"disambiguationData":[TD([[makeQuery(id+"F22.imprint","IMPRINT",EDGE,{"derivedFrom":subQ0}),1.0]])]});}
            var Q1;
            {var subQ0=sQuery(id+"F22.wireOp",EDGE,"E90.left");Q1=makeQuery(id+"F22.imprint","IMPRINT",FACE,{"disambiguationData":[TD([[makeQuery(id+"F22.imprint","IMPRINT",EDGE,{"derivedFrom":subQ0}),-1.0]])]});}
            var Q2;
            {var subQ0=sQuery(id+"F22.wireOp",EDGE,"E89.right");Q2=makeQuery(id+"F22.imprint","IMPRINT",FACE,{"disambiguationData":[TD([[makeQuery(id+"F22.imprint","IMPRINT",EDGE,{"derivedFrom":subQ0}),-1.0]])]});}
            var Q3;
            {var subQ0=sQuery(id+"F22.wireOp",EDGE,"E89.left");Q3=makeQuery(id+"F22.imprint","IMPRINT",FACE,{"disambiguationData":[TD([[makeQuery(id+"F22.imprint","IMPRINT",EDGE,{"derivedFrom":subQ0}),1.0]])]});}
            extrude(context, id + "F24", {"entities" : qUnion([Q0, Q1, Q2, Q3]), "operationType" : NewBodyOperationType.ADD, "oppositeDirection" : true, "depth" : 9.5 * mm});
        }
        {
            var Q0;
            {var subQ0=sQuery(id+"F22.wireOp",EDGE,"E128");Q0=makeQuery(id+"F22.imprint","IMPRINT",FACE,{"disambiguationData":[TD([[makeQuery(id+"F22.imprint","IMPRINT",EDGE,{"derivedFrom":subQ0}),-1.0]])]});}
            var Q1;
            {var subQ0=sQuery(id+"F22.wireOp",EDGE,"E129");Q1=makeQuery(id+"F22.imprint","IMPRINT",FACE,{"disambiguationData":[TD([[makeQuery(id+"F22.imprint","IMPRINT",EDGE,{"derivedFrom":subQ0}),-1.0]])]});}
            extrude(context, id + "F25", {"entities" : qUnion([Q0, Q1]), "operationType" : NewBodyOperationType.ADD, "oppositeDirection" : true, "depth" : 8 * mm});
        }
        {
            var Q0;
            Q0=makeQuery(id+"F23.opExtrude","SWEPT_EDGE",EDGE,{"disambiguationData":[OSD([sQuery(id+"F22.wireOp",EDGE,"fd68ecca-2644-4456-80ce-795f9b9d7dc50.MirrorCS"),sQuery(id+"F22.wireOp",EDGE,"fcdf2fa3-4911-45db-a72c-c9a4e220fdae0.MirrorCS")])]});
            var Q1;
            Q1=makeQuery(id+"F23.opExtrude","SWEPT_EDGE",EDGE,{"disambiguationData":[OSD([sQuery(id+"F22.wireOp",EDGE,"fd68ecca-2644-4456-80ce-795f9b9d7dc50.MirrorCS"),sQuery(id+"F22.wireOp",EDGE,"e47788c3-db41-4284-80c2-0dbcda57038b0.MirrorCS")])]});
            var Q2;
            Q2=makeQuery(id+"F23.opExtrude","SWEPT_EDGE",EDGE,{"disambiguationData":[OSD([sQuery(id+"F22.wireOp",EDGE,"E105.top"),sQuery(id+"F22.wireOp",EDGE,"E105.right")])]});
            var Q3;
            Q3=makeQuery(id+"F23.opExtrude","SWEPT_EDGE",EDGE,{"disambiguationData":[OSD([sQuery(id+"F22.wireOp",EDGE,"9299e7e0-0858-453c-8674-e1bf03801ec8.0"),sQuery(id+"F22.wireOp",EDGE,"E105.bottom"),sQuery(id+"F22.wireOp",EDGE,"E105.right")])]});
            var Q4;
            Q4=makeQuery(id+"F23.opExtrude","SWEPT_EDGE",EDGE,{"disambiguationData":[OSD([sQuery(id+"F22.wireOp",EDGE,"E100.bottom"),sQuery(id+"F22.wireOp",EDGE,"E100.right")])]});
            var Q5;
            Q5=makeQuery(id+"F23.opExtrude","SWEPT_EDGE",EDGE,{"disambiguationData":[OSD([sQuery(id+"F22.wireOp",EDGE,"E100.top"),sQuery(id+"F22.wireOp",EDGE,"E100.right")])]});
            var Q6;
            Q6=makeQuery(id+"F23.opExtrude","SWEPT_EDGE",EDGE,{"disambiguationData":[OSD([sQuery(id+"F22.wireOp",EDGE,"E114.MirrorCS"),sQuery(id+"F22.wireOp",EDGE,"E115.MirrorCS")])]});
            var Q7;
            Q7=makeQuery(id+"F23.opExtrude","SWEPT_EDGE",EDGE,{"disambiguationData":[OSD([sQuery(id+"F22.wireOp",EDGE,"E113.MirrorCS"),sQuery(id+"F22.wireOp",EDGE,"E114.MirrorCS")])]});
            var Q8;
            Q8=makeQuery(id+"F23.opExtrude","SWEPT_EDGE",EDGE,{"disambiguationData":[OSD([sQuery(id+"F22.wireOp",EDGE,"E118.MirrorCS"),sQuery(id+"F22.wireOp",EDGE,"E121.MirrorCS")])]});
            var Q9;
            Q9=makeQuery(id+"F23.opExtrude","SWEPT_EDGE",EDGE,{"disambiguationData":[OSD([sQuery(id+"F22.wireOp",EDGE,"E120.MirrorCS"),sQuery(id+"F22.wireOp",EDGE,"E121.MirrorCS")])]});
            var Q10;
            Q10=makeQuery(id+"F23.opExtrude","SWEPT_EDGE",EDGE,{"disambiguationData":[OSD([sQuery(id+"F22.wireOp",EDGE,"E117.top"),sQuery(id+"F22.wireOp",EDGE,"E117.left")])]});
            var Q11;
            Q11=makeQuery(id+"F23.opExtrude","SWEPT_EDGE",EDGE,{"disambiguationData":[OSD([sQuery(id+"F22.wireOp",EDGE,"E117.bottom"),sQuery(id+"F22.wireOp",EDGE,"E117.left")])]});
            var Q12;
            Q12=makeQuery(id+"F24.opExtrude","SWEPT_EDGE",EDGE,{"disambiguationData":[OSD([sQuery(id+"F22.wireOp",EDGE,"E90.bottom"),sQuery(id+"F22.wireOp",EDGE,"E90.left"),sQuery(id+"F22.wireOp",EDGE,"E123.MirrorCS")])]});
            var Q13;
            Q13=makeQuery(id+"F24.opExtrude","SWEPT_EDGE",EDGE,{"disambiguationData":[OSD([sQuery(id+"F22.wireOp",EDGE,"E89.top"),sQuery(id+"F22.wireOp",EDGE,"E89.left"),sQuery(id+"F22.wireOp",EDGE,"E116")])]});
            var Q14;
            Q14=makeQuery(id+"F24.opExtrude","SWEPT_EDGE",EDGE,{"disambiguationData":[OSD([sQuery(id+"F22.wireOp",EDGE,"E89.bottom"),sQuery(id+"F22.wireOp",EDGE,"E89.right"),sQuery(id+"F22.wireOp",EDGE,"E112.MirrorCS")])]});
            var Q15;
            Q15=makeQuery(id+"F24.opExtrude","SWEPT_EDGE",EDGE,{"disambiguationData":[OSD([sQuery(id+"F22.wireOp",EDGE,"E90.top"),sQuery(id+"F22.wireOp",EDGE,"E90.right"),sQuery(id+"F22.wireOp",EDGE,"E106")])]});
            var Q16;
            Q16=makeQuery(id+"F24.opExtrude","SWEPT_EDGE",EDGE,{"disambiguationData":[OSD([sQuery(id+"F22.wireOp",EDGE,"E89.top"),sQuery(id+"F22.wireOp",EDGE,"E89.right"),sQuery(id+"F22.wireOp",EDGE,"E111.MirrorCS")])]});
            var Q17;
            Q17=makeQuery(id+"F24.opExtrude","SWEPT_EDGE",EDGE,{"disambiguationData":[OSD([sQuery(id+"F22.wireOp",EDGE,"E90.bottom"),sQuery(id+"F22.wireOp",EDGE,"E90.right"),sQuery(id+"F22.wireOp",EDGE,"E101")])]});
            var Q18;
            Q18=makeQuery(id+"F24.opExtrude","SWEPT_EDGE",EDGE,{"disambiguationData":[OSD([sQuery(id+"F22.wireOp",EDGE,"E89.bottom"),sQuery(id+"F22.wireOp",EDGE,"E89.left"),sQuery(id+"F22.wireOp",EDGE,"E122")])]});
            var Q19;
            Q19=makeQuery(id+"F24.opExtrude","SWEPT_EDGE",EDGE,{"disambiguationData":[OSD([sQuery(id+"F22.wireOp",EDGE,"E90.top"),sQuery(id+"F22.wireOp",EDGE,"E90.left"),sQuery(id+"F22.wireOp",EDGE,"E124.MirrorCS")])]});
            fillet(context, id + "F26", {"entities" : qUnion([Q0, Q1, Q2, Q3, Q4, Q5, Q6, Q7, Q8, Q9, Q10, Q11, Q12, Q13, Q14, Q15, Q16, Q17, Q18, Q19]), "radius" : 5 * mm, "tangentPropagation" : true, "allowEdgeOverflow" : false});
        }
        {
            var Q0;
            Q0=makeQuery(id+"F24.opExtrude","CAP_FACE",FACE,{"disambiguationData":[OSD([sQuery(id+"F22.wireOp",EDGE,"E89.bottom"),sQuery(id+"F22.wireOp",EDGE,"E89.top"),sQuery(id+"F22.wireOp",EDGE,"E89.left"),sQuery(id+"F22.wireOp",EDGE,"E131.MirrorCS")])],"isStart":false});
            var sketch = newSketch(context, id + "F27", { "sketchPlane" : qUnion([Q0])});
            skLineSegment(sketch, "E132.0", {"start": v(63.19, 54) * mm, "end": v(63.19, 42) * mm});
            skLineSegment(sketch, "E133.0", {"start": v(63.19, 98) * mm, "end": v(63.19, 86) * mm});
            skLineSegment(sketch, "E134.0", {"start": v(70.19, 98) * mm, "end": v(70.19, 86) * mm});
            skLineSegment(sketch, "E135", {"start": v(70.19, 42) * mm, "end": v(63.19, 42) * mm});
            skLineSegment(sketch, "E136", {"start": v(63.19, 54) * mm, "end": v(70.19, 54) * mm});
            skLineSegment(sketch, "E137", {"start": v(70.19, 86) * mm, "end": v(63.19, 86) * mm});
            skLineSegment(sketch, "E138", {"start": v(63.19, 98) * mm, "end": v(70.19, 98) * mm});
            skLineSegment(sketch, "E139.0.0", {"start": v(63.19, 54) * mm, "end": v(57.69, 54) * mm});
            skArc(sketch, "E139.0.1", {"start": v(57.69, 54) * mm, "mid": v(54.15, 52.54) * mm, "end": v(52.69, 49) * mm});
            skLineSegment(sketch, "E139.0.2", {"start": v(52.69, 49) * mm, "end": v(52.69, 47) * mm});
            skArc(sketch, "E139.0.3", {"start": v(52.69, 47) * mm, "mid": v(54.15, 43.46) * mm, "end": v(57.69, 42) * mm});
            skLineSegment(sketch, "E139.0.4", {"start": v(57.69, 42) * mm, "end": v(63.19, 42) * mm});
            skLineSegment(sketch, "E139.0.5", {"start": v(63.19, 42) * mm, "end": v(63.19, 54) * mm});
            skLineSegment(sketch, "E140.0.0", {"start": v(63.19, 98) * mm, "end": v(57.69, 98) * mm});
            skArc(sketch, "E140.0.1", {"start": v(57.69, 98) * mm, "mid": v(54.15, 96.54) * mm, "end": v(52.69, 93) * mm});
            skLineSegment(sketch, "E140.0.2", {"start": v(52.69, 93) * mm, "end": v(52.69, 91) * mm});
            skArc(sketch, "E140.0.3", {"start": v(52.69, 91) * mm, "mid": v(54.15, 87.46) * mm, "end": v(57.69, 86) * mm});
            skLineSegment(sketch, "E140.0.4", {"start": v(57.69, 86) * mm, "end": v(63.19, 86) * mm});
            skLineSegment(sketch, "E140.0.5", {"start": v(63.19, 86) * mm, "end": v(63.19, 98) * mm});
            skLineSegment(sketch, "E140.1.0", {"start": v(80.69, 91) * mm, "end": v(80.69, 93) * mm});
            skArc(sketch, "E140.1.1", {"start": v(80.69, 93) * mm, "mid": v(79.22, 96.54) * mm, "end": v(75.69, 98) * mm});
            skLineSegment(sketch, "E140.1.2", {"start": v(75.69, 98) * mm, "end": v(70.19, 98) * mm});
            skLineSegment(sketch, "E140.1.4", {"start": v(70.19, 86) * mm, "end": v(75.69, 86) * mm});
            skArc(sketch, "E140.1.5", {"start": v(75.69, 86) * mm, "mid": v(79.22, 87.46) * mm, "end": v(80.69, 91) * mm});
            skSolve(sketch);
        }
        {
            var Q0;
            {var subQ3=sQuery(id+"F22.wireOp",EDGE,"E131.MirrorCS");Q0=makeQuery(id+"F27.imprint","IMPRINT",FACE,{"disambiguationData":[TD([[makeQuery(id+"F27.imprint","IMPRINT",EDGE,{"derivedFrom":makeQuery(id+"F24.opExtrude","CAP_EDGE",EDGE,{"disambiguationData":[OSD([subQ3])],"isStart":false})}),1.0]])]});}
            var Q1;
            Q1=makeQuery(id+"F27.imprint","IMPRINT",FACE,{"disambiguationData":[TD([[makeQuery(id+"F27.imprint","IMPRINT",EDGE,{"derivedFrom":sQuery(id+"F27.wireOp",EDGE,"E132.0")}),1.0]])]});
            var Q2;
            Q2=makeQuery(id+"F27.imprint","IMPRINT",FACE,{"disambiguationData":[TD([[makeQuery(id+"F27.imprint","IMPRINT",EDGE,{"derivedFrom":sQuery(id+"F27.wireOp",EDGE,"E133.0")}),1.0]])]});
            var Q3;
            Q3=makeQuery(id+"F27.imprint","IMPRINT",FACE,{"disambiguationData":[TD([[makeQuery(id+"F27.imprint","IMPRINT",EDGE,{"derivedFrom":sQuery(id+"F27.wireOp",EDGE,"E135")}),-1.0]])]});
            var Q4;
            Q4=makeQuery(id+"F27.imprint","IMPRINT",FACE,{"disambiguationData":[TD([[makeQuery(id+"F27.imprint","IMPRINT",EDGE,{"derivedFrom":sQuery(id+"F27.wireOp",EDGE,"E139.0.0")}),1.0]])]});
            var Q5;
            Q5=makeQuery(id+"F27.imprint","IMPRINT",FACE,{"disambiguationData":[TD([[makeQuery(id+"F27.imprint","IMPRINT",EDGE,{"derivedFrom":sQuery(id+"F27.wireOp",EDGE,"E140.1.0")}),1.0]])]});
            var Q6;
            Q6=makeQuery(id+"F27.imprint","IMPRINT",FACE,{"disambiguationData":[TD([[makeQuery(id+"F27.imprint","IMPRINT",EDGE,{"derivedFrom":sQuery(id+"F27.wireOp",EDGE,"E137")}),-1.0]])]});
            var Q7;
            Q7=makeQuery(id+"F27.imprint","IMPRINT",FACE,{"disambiguationData":[TD([[makeQuery(id+"F27.imprint","IMPRINT",EDGE,{"derivedFrom":sQuery(id+"F27.wireOp",EDGE,"E140.0.0")}),1.0]])]});
            extrude(context, id + "F28", {"entities" : qUnion([Q0, Q1, Q2, Q3, Q4, Q5, Q6, Q7]), "depth" : 6 * mm});
        }
        {
            var Q0;
            Q0=makeQuery(id+"F28.opExtrude","CAP_FACE",FACE,{"disambiguationData":[OSD([sQuery(id+"F22.wireOp",EDGE,"E89.bottom"),sQuery(id+"F22.wireOp",EDGE,"E89.top"),sQuery(id+"F22.wireOp",EDGE,"E89.left"),sQuery(id+"F22.wireOp",EDGE,"E116"),sQuery(id+"F22.wireOp",EDGE,"E122"),sQuery(id+"F22.wireOp",EDGE,"E131.MirrorCS"),sQuery(id+"F27.wireOp",EDGE,"E135"),sQuery(id+"F27.wireOp",EDGE,"E136"),sQuery(id+"F27.wireOp",EDGE,"E139.0.0"),sQuery(id+"F27.wireOp",EDGE,"E139.0.1"),sQuery(id+"F27.wireOp",EDGE,"E139.0.2"),sQuery(id+"F27.wireOp",EDGE,"E139.0.3"),sQuery(id+"F27.wireOp",EDGE,"E139.0.4")])],"isStart":false});
            var sketch = newSketch(context, id + "F29", { "sketchPlane" : qUnion([Q0])});
            skPoint(sketch, "E141.0", {"position": v(74.69, 92) * mm});
            skPoint(sketch, "E141.1", {"position": v(58.69, 92) * mm});
            skPoint(sketch, "E141.2", {"position": v(74.69, 48) * mm});
            skPoint(sketch, "E141.3", {"position": v(58.69, 48) * mm});
            skCircle(sketch, "E142.cCircle", {"center": v(74.69, 48) * mm, "radius": 3.1 * mm, "construction": true});
            skLineSegment(sketch, "E142.0", {"start": v(71.59, 46.21) * mm, "end": v(71.59, 49.79) * mm});
            skLineSegment(sketch, "E142.1", {"start": v(71.59, 49.79) * mm, "end": v(74.69, 51.58) * mm});
            skLineSegment(sketch, "E142.2", {"start": v(74.69, 51.58) * mm, "end": v(77.79, 49.79) * mm});
            skLineSegment(sketch, "E142.3", {"start": v(77.79, 49.79) * mm, "end": v(77.79, 46.21) * mm});
            skLineSegment(sketch, "E142.4", {"start": v(77.79, 46.21) * mm, "end": v(74.69, 44.42) * mm});
            skLineSegment(sketch, "E142.5", {"start": v(74.69, 44.42) * mm, "end": v(71.59, 46.21) * mm});
            skPoint(sketch, "E142.0.midPoint", {"position": v(71.59, 48) * mm});
            skCircle(sketch, "E143.cCircle", {"center": v(58.69, 48) * mm, "radius": 3.1 * mm, "construction": true});
            skLineSegment(sketch, "E143.0", {"start": v(61.79, 49.79) * mm, "end": v(61.79, 46.21) * mm});
            skLineSegment(sketch, "E143.1", {"start": v(61.79, 46.21) * mm, "end": v(58.69, 44.42) * mm});
            skLineSegment(sketch, "E143.2", {"start": v(58.69, 44.42) * mm, "end": v(55.59, 46.21) * mm});
            skLineSegment(sketch, "E143.3", {"start": v(55.59, 46.21) * mm, "end": v(55.59, 49.79) * mm});
            skLineSegment(sketch, "E143.4", {"start": v(55.59, 49.79) * mm, "end": v(58.69, 51.58) * mm});
            skLineSegment(sketch, "E143.5", {"start": v(58.69, 51.58) * mm, "end": v(61.79, 49.79) * mm});
            skPoint(sketch, "E143.0.midPoint", {"position": v(61.79, 48) * mm});
            skCircle(sketch, "E144.cCircle", {"center": v(74.69, 92) * mm, "radius": 3.1 * mm, "construction": true});
            skLineSegment(sketch, "E144.0", {"start": v(77.79, 93.79) * mm, "end": v(77.79, 90.21) * mm});
            skLineSegment(sketch, "E144.1", {"start": v(77.79, 90.21) * mm, "end": v(74.69, 88.42) * mm});
            skLineSegment(sketch, "E144.2", {"start": v(74.69, 88.42) * mm, "end": v(71.59, 90.21) * mm});
            skLineSegment(sketch, "E144.3", {"start": v(71.59, 90.21) * mm, "end": v(71.59, 93.79) * mm});
            skLineSegment(sketch, "E144.4", {"start": v(71.59, 93.79) * mm, "end": v(74.69, 95.58) * mm});
            skLineSegment(sketch, "E144.5", {"start": v(74.69, 95.58) * mm, "end": v(77.79, 93.79) * mm});
            skPoint(sketch, "E144.0.midPoint", {"position": v(77.79, 92) * mm});
            skCircle(sketch, "E145.cCircle", {"center": v(58.69, 92) * mm, "radius": 3.1 * mm, "construction": true});
            skLineSegment(sketch, "E145.0", {"start": v(61.79, 93.79) * mm, "end": v(61.79, 90.21) * mm});
            skLineSegment(sketch, "E145.1", {"start": v(61.79, 90.21) * mm, "end": v(58.69, 88.42) * mm});
            skLineSegment(sketch, "E145.2", {"start": v(58.69, 88.42) * mm, "end": v(55.59, 90.21) * mm});
            skLineSegment(sketch, "E145.3", {"start": v(55.59, 90.21) * mm, "end": v(55.59, 93.79) * mm});
            skLineSegment(sketch, "E145.4", {"start": v(55.59, 93.79) * mm, "end": v(58.69, 95.58) * mm});
            skLineSegment(sketch, "E145.5", {"start": v(58.69, 95.58) * mm, "end": v(61.79, 93.79) * mm});
            skPoint(sketch, "E145.0.midPoint", {"position": v(61.79, 92) * mm});
            skSolve(sketch);
        }
        {
            var Q0;
            Q0=sQuery(id+"F29.wireOp",VERTEX,"E141.2");
            var Q1;
            Q1=sQuery(id+"F29.wireOp",VERTEX,"E141.3");
            var Q2;
            Q2=sQuery(id+"F29.wireOp",VERTEX,"E141.1");
            var Q3;
            Q3=sQuery(id+"F29.wireOp",VERTEX,"E141.0");
            var Q4;
            Q4=makeQuery(id+"F23.opExtrude","SWEPT_BODY",BODY,{"disambiguationData":[OSD([sQuery(id+"F22.wireOp",EDGE,"E88.0"),sQuery(id+"F22.wireOp",EDGE,"E88.1"),sQuery(id+"F22.wireOp",EDGE,"E88.2"),sQuery(id+"F22.wireOp",EDGE,"E88.3"),sQuery(id+"F22.wireOp",EDGE,"E89.bottom"),sQuery(id+"F22.wireOp",EDGE,"E89.top"),sQuery(id+"F22.wireOp",EDGE,"E90.bottom"),sQuery(id+"F22.wireOp",EDGE,"E90.top"),sQuery(id+"F22.wireOp",EDGE,"E100.bottom"),sQuery(id+"F22.wireOp",EDGE,"E100.top"),sQuery(id+"F22.wireOp",EDGE,"E100.right"),sQuery(id+"F22.wireOp",EDGE,"E101"),sQuery(id+"F22.wireOp",EDGE,"E106"),sQuery(id+"F22.wireOp",EDGE,"E111.MirrorCS"),sQuery(id+"F22.wireOp",EDGE,"E112.MirrorCS"),sQuery(id+"F22.wireOp",EDGE,"E113.MirrorCS"),sQuery(id+"F22.wireOp",EDGE,"E114.MirrorCS"),sQuery(id+"F22.wireOp",EDGE,"E115.MirrorCS"),sQuery(id+"F22.wireOp",EDGE,"E116"),sQuery(id+"F22.wireOp",EDGE,"E117.bottom"),sQuery(id+"F22.wireOp",EDGE,"E117.top"),sQuery(id+"F22.wireOp",EDGE,"E117.left"),sQuery(id+"F22.wireOp",EDGE,"E118.MirrorCS"),sQuery(id+"F22.wireOp",EDGE,"E120.MirrorCS"),sQuery(id+"F22.wireOp",EDGE,"E121.MirrorCS"),sQuery(id+"F22.wireOp",EDGE,"E122"),sQuery(id+"F22.wireOp",EDGE,"E123.MirrorCS"),sQuery(id+"F22.wireOp",EDGE,"E124.MirrorCS")])]});
            var Q5;
            Q5=makeQuery(id+"F28.opExtrude","SWEPT_BODY",BODY,{"disambiguationData":[OSD([sQuery(id+"F22.wireOp",EDGE,"E89.bottom"),sQuery(id+"F22.wireOp",EDGE,"E89.top"),sQuery(id+"F22.wireOp",EDGE,"E89.left"),sQuery(id+"F22.wireOp",EDGE,"E116"),sQuery(id+"F22.wireOp",EDGE,"E122"),sQuery(id+"F22.wireOp",EDGE,"E131.MirrorCS"),sQuery(id+"F27.wireOp",EDGE,"E135"),sQuery(id+"F27.wireOp",EDGE,"E136"),sQuery(id+"F27.wireOp",EDGE,"E139.0.0"),sQuery(id+"F27.wireOp",EDGE,"E139.0.1"),sQuery(id+"F27.wireOp",EDGE,"E139.0.2"),sQuery(id+"F27.wireOp",EDGE,"E139.0.3"),sQuery(id+"F27.wireOp",EDGE,"E139.0.4")])]});
            var Q6;
            Q6=makeQuery(id+"F28.opExtrude","SWEPT_BODY",BODY,{"disambiguationData":[OSD([sQuery(id+"F27.wireOp",EDGE,"E137"),sQuery(id+"F27.wireOp",EDGE,"E138"),sQuery(id+"F27.wireOp",EDGE,"E140.0.0"),sQuery(id+"F27.wireOp",EDGE,"E140.0.1"),sQuery(id+"F27.wireOp",EDGE,"E140.0.2"),sQuery(id+"F27.wireOp",EDGE,"E140.0.3"),sQuery(id+"F27.wireOp",EDGE,"E140.0.4"),sQuery(id+"F27.wireOp",EDGE,"E140.1.0"),sQuery(id+"F27.wireOp",EDGE,"E140.1.1"),sQuery(id+"F27.wireOp",EDGE,"E140.1.2"),sQuery(id+"F27.wireOp",EDGE,"E140.1.4"),sQuery(id+"F27.wireOp",EDGE,"E140.1.5")])]});
            hole(context, id + "F30", {"style" : HoleStyle.SIMPLE, "endStyle" : HoleEndStyle.THROUGH, "standardTappedOrClearance" : lookupTablePath({ "standard" : "ISO", "fit" : "Normal", "size" : "M3", "type" : "Clearance" }), "standardBlindInLast" : lookupTablePath({ "fit" : "Standard", "standard" : "ISO", "size" : "M3", "type" : "Clearance" }), "holeDiameter" : 3.3 * mm, "isTappedThrough" : true, "tappedDepth" : 12 * mm, "tapClearance" : 3, "locations" : qUnion([Q0, Q1, Q2, Q3]), "scope" : qUnion([Q4, Q5, Q6])});
        }
        {
            var Q0;
            Q0=makeQuery(id+"F29.imprint","IMPRINT",FACE,{"disambiguationData":[TD([[makeQuery(id+"F29.imprint","IMPRINT",EDGE,{"derivedFrom":sQuery(id+"F29.wireOp",EDGE,"E142.0")}),-1.0]])]});
            var Q1;
            Q1=makeQuery(id+"F29.imprint","IMPRINT",FACE,{"disambiguationData":[TD([[makeQuery(id+"F29.imprint","IMPRINT",EDGE,{"derivedFrom":sQuery(id+"F29.wireOp",EDGE,"E145.0")}),-1.0]])]});
            var Q2;
            Q2=makeQuery(id+"F29.imprint","IMPRINT",FACE,{"disambiguationData":[TD([[makeQuery(id+"F29.imprint","IMPRINT",EDGE,{"derivedFrom":sQuery(id+"F29.wireOp",EDGE,"E143.0")}),-1.0]])]});
            var Q3;
            Q3=makeQuery(id+"F29.imprint","IMPRINT",FACE,{"disambiguationData":[TD([[makeQuery(id+"F29.imprint","IMPRINT",EDGE,{"derivedFrom":sQuery(id+"F29.wireOp",EDGE,"E144.0")}),-1.0]])]});
            extrude(context, id + "F31", {"entities" : qUnion([Q0, Q1, Q2, Q3]), "operationType" : NewBodyOperationType.REMOVE, "oppositeDirection" : true, "depth" : 3 * mm});
        }
    });
